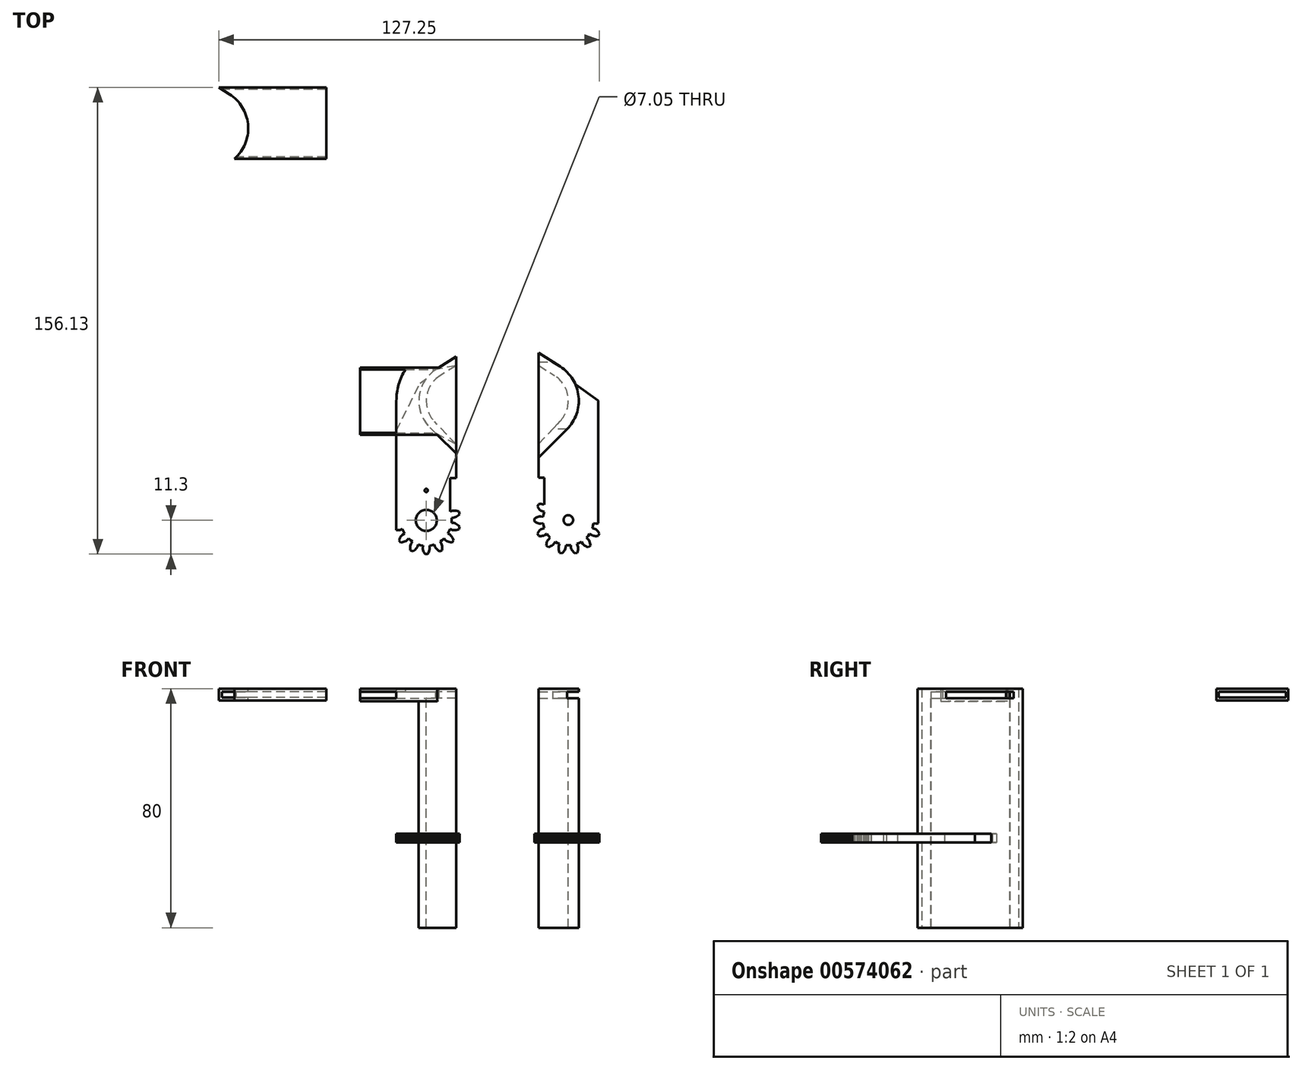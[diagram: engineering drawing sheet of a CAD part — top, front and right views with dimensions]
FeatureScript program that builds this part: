
annotation { "Feature Type Name" : "Feature", "Feature Type Description" : "" }
export const myFeature = defineFeature(function(context is Context, id is Id, definition is map)
    precondition{}
    {
        {
            var Q0;
            Q0=qCreatedBy(makeId("Top.planeOp"),FACE);
            var sketch = newSketch(context, id + "F0", { "sketchPlane" : qUnion([Q0])});
            skLineSegment(sketch, "E0", {"start": v(-11.89, -38.22) * mm, "end": v(-11.08, -38.37) * mm});
            skLineSegment(sketch, "E1", {"start": v(-11.08, -38.37) * mm, "end": v(-11.18, -39.18) * mm});
            skLineSegment(sketch, "E2", {"start": v(-11.18, -39.18) * mm, "end": v(-11.15, -39.59) * mm});
            skLineSegment(sketch, "E3", {"start": v(-11.15, -39.59) * mm, "end": v(-11.05, -40) * mm});
            skLineSegment(sketch, "E4", {"start": v(-11.05, -40) * mm, "end": v(-10.9, -40.42) * mm});
            skLineSegment(sketch, "E5", {"start": v(-10.9, -40.42) * mm, "end": v(-10.7, -40.84) * mm});
            skLineSegment(sketch, "E6", {"start": v(-10.7, -40.84) * mm, "end": v(-10.46, -41.25) * mm});
            skLineSegment(sketch, "E7", {"start": v(-10.46, -41.25) * mm, "end": v(-9.54, -41.25) * mm});
            skLineSegment(sketch, "E8", {"start": v(-9.54, -41.25) * mm, "end": v(-9.3, -40.84) * mm});
            skLineSegment(sketch, "E9", {"start": v(-9.3, -40.84) * mm, "end": v(-9.1, -40.42) * mm});
            skLineSegment(sketch, "E10", {"start": v(-9.1, -40.42) * mm, "end": v(-8.95, -40) * mm});
            skLineSegment(sketch, "E11", {"start": v(-8.95, -40) * mm, "end": v(-8.85, -39.59) * mm});
            skLineSegment(sketch, "E12", {"start": v(-8.85, -39.59) * mm, "end": v(-8.82, -39.18) * mm});
            skLineSegment(sketch, "E13", {"start": v(-8.82, -39.18) * mm, "end": v(-8.92, -38.37) * mm});
            skLineSegment(sketch, "E14", {"start": v(-8.92, -38.37) * mm, "end": v(-8.11, -38.22) * mm});
            skLineSegment(sketch, "E15", {"start": v(-8.11, -38.22) * mm, "end": v(-8.11, -38.22) * mm});
            skLineSegment(sketch, "E16", {"start": v(-8.11, -38.22) * mm, "end": v(-7.32, -38) * mm});
            skLineSegment(sketch, "E17", {"start": v(-7.32, -38) * mm, "end": v(-7.06, -38.78) * mm});
            skLineSegment(sketch, "E18", {"start": v(-7.06, -38.78) * mm, "end": v(-6.86, -39.13) * mm});
            skLineSegment(sketch, "E19", {"start": v(-6.86, -39.13) * mm, "end": v(-6.58, -39.46) * mm});
            skLineSegment(sketch, "E20", {"start": v(-6.58, -39.46) * mm, "end": v(-6.26, -39.77) * mm});
            skLineSegment(sketch, "E21", {"start": v(-6.26, -39.77) * mm, "end": v(-5.9, -40.06) * mm});
            skLineSegment(sketch, "E22", {"start": v(-5.9, -40.06) * mm, "end": v(-5.5, -40.33) * mm});
            skLineSegment(sketch, "E23", {"start": v(-5.5, -40.33) * mm, "end": v(-4.68, -39.94) * mm});
            skLineSegment(sketch, "E24", {"start": v(-4.68, -39.94) * mm, "end": v(-4.65, -39.46) * mm});
            skLineSegment(sketch, "E25", {"start": v(-4.65, -39.46) * mm, "end": v(-4.65, -39) * mm});
            skLineSegment(sketch, "E26", {"start": v(-4.7, -38.55) * mm, "end": v(-4.78, -38.13) * mm});
            skLineSegment(sketch, "E27", {"start": v(-4.78, -38.13) * mm, "end": v(-4.93, -37.75) * mm});
            skLineSegment(sketch, "E28", {"start": v(-4.93, -37.75) * mm, "end": v(-5.38, -37.07) * mm});
            skLineSegment(sketch, "E29", {"start": v(-4.09, -36.04) * mm, "end": v(-3.52, -36.62) * mm});
            skLineSegment(sketch, "E30", {"start": v(-3.18, -36.86) * mm, "end": v(-2.8, -37.04) * mm});
            skLineSegment(sketch, "E31", {"start": v(-2.37, -37.18) * mm, "end": v(-1.92, -37.28) * mm});
            skLineSegment(sketch, "E32", {"start": v(-1.05, -36.2) * mm, "end": v(-1.25, -35.78) * mm});
            skLineSegment(sketch, "E33", {"start": v(-1.25, -35.78) * mm, "end": v(-1.49, -35.4) * mm});
            skLineSegment(sketch, "E34", {"start": v(-2.05, -34.78) * mm, "end": v(-2.75, -34.36) * mm});
            skLineSegment(sketch, "E35", {"start": v(-2.03, -32.87) * mm, "end": v(-1.27, -33.15) * mm});
            skLineSegment(sketch, "E36", {"start": v(-20, -33.15) * mm, "end": v(-19.57, -33.2) * mm});
            skLineSegment(sketch, "E37", {"start": v(-19.57, -33.2) * mm, "end": v(-19.14, -33.22) * mm});
            skLineSegment(sketch, "E38", {"start": v(-19.14, -33.22) * mm, "end": v(-18.73, -33.15) * mm});
            skLineSegment(sketch, "E39", {"start": v(-18.73, -33.15) * mm, "end": v(-17.97, -32.87) * mm});
            skLineSegment(sketch, "E40", {"start": v(-17.97, -32.87) * mm, "end": v(-17.64, -33.63) * mm});
            skLineSegment(sketch, "E41", {"start": v(-17.64, -33.63) * mm, "end": v(-17.65, -33.63) * mm});
            skLineSegment(sketch, "E42", {"start": v(-17.65, -33.63) * mm, "end": v(-17.25, -34.36) * mm});
            skLineSegment(sketch, "E43", {"start": v(-17.25, -34.36) * mm, "end": v(-17.95, -34.78) * mm});
            skLineSegment(sketch, "E44", {"start": v(-17.95, -34.78) * mm, "end": v(-18.25, -35.06) * mm});
            skLineSegment(sketch, "E45", {"start": v(-18.25, -35.06) * mm, "end": v(-18.51, -35.4) * mm});
            skLineSegment(sketch, "E46", {"start": v(-18.51, -35.4) * mm, "end": v(-18.75, -35.78) * mm});
            skLineSegment(sketch, "E47", {"start": v(-18.75, -35.78) * mm, "end": v(-18.95, -36.2) * mm});
            skLineSegment(sketch, "E48", {"start": v(-18.95, -36.2) * mm, "end": v(-19.12, -36.64) * mm});
            skLineSegment(sketch, "E49", {"start": v(-19.12, -36.64) * mm, "end": v(-18.55, -37.36) * mm});
            skLineSegment(sketch, "E50", {"start": v(-18.55, -37.36) * mm, "end": v(-18.08, -37.28) * mm});
            skLineSegment(sketch, "E51", {"start": v(-18.08, -37.28) * mm, "end": v(-17.63, -37.18) * mm});
            skLineSegment(sketch, "E52", {"start": v(-17.63, -37.18) * mm, "end": v(-17.2, -37.04) * mm});
            skLineSegment(sketch, "E53", {"start": v(-17.2, -37.04) * mm, "end": v(-16.82, -36.86) * mm});
            skLineSegment(sketch, "E54", {"start": v(-16.82, -36.86) * mm, "end": v(-16.48, -36.62) * mm});
            skLineSegment(sketch, "E55", {"start": v(-16.48, -36.62) * mm, "end": v(-15.91, -36.04) * mm});
            skLineSegment(sketch, "E56", {"start": v(-15.91, -36.04) * mm, "end": v(-15.3, -36.58) * mm});
            skLineSegment(sketch, "E57", {"start": v(-15.3, -36.58) * mm, "end": v(-15.3, -36.58) * mm});
            skLineSegment(sketch, "E58", {"start": v(-15.3, -36.58) * mm, "end": v(-14.62, -37.07) * mm});
            skLineSegment(sketch, "E59", {"start": v(-14.62, -37.07) * mm, "end": v(-15.07, -37.75) * mm});
            skLineSegment(sketch, "E60", {"start": v(-15.07, -37.75) * mm, "end": v(-15.22, -38.13) * mm});
            skLineSegment(sketch, "E61", {"start": v(-15.22, -38.13) * mm, "end": v(-15.3, -38.55) * mm});
            skLineSegment(sketch, "E62", {"start": v(-15.3, -38.55) * mm, "end": v(-15.35, -39) * mm});
            skLineSegment(sketch, "E63", {"start": v(-15.35, -39) * mm, "end": v(-15.35, -39.46) * mm});
            skLineSegment(sketch, "E64", {"start": v(-15.35, -39.46) * mm, "end": v(-15.32, -39.94) * mm});
            skLineSegment(sketch, "E65", {"start": v(-15.32, -39.94) * mm, "end": v(-14.5, -40.33) * mm});
            skLineSegment(sketch, "E66", {"start": v(-14.5, -40.33) * mm, "end": v(-14.1, -40.06) * mm});
            skLineSegment(sketch, "E67", {"start": v(-14.1, -40.06) * mm, "end": v(-13.74, -39.77) * mm});
            skLineSegment(sketch, "E68", {"start": v(-13.74, -39.77) * mm, "end": v(-13.42, -39.46) * mm});
            skLineSegment(sketch, "E69", {"start": v(-13.42, -39.46) * mm, "end": v(-13.14, -39.13) * mm});
            skLineSegment(sketch, "E70", {"start": v(-13.14, -39.13) * mm, "end": v(-12.94, -38.78) * mm});
            skLineSegment(sketch, "E71", {"start": v(-12.94, -38.78) * mm, "end": v(-12.68, -38) * mm});
            skLineSegment(sketch, "E72", {"start": v(-12.68, -38) * mm, "end": v(-11.89, -38.22) * mm});
            skLineSegment(sketch, "E73", {"start": v(-11.89, -38.22) * mm, "end": v(-11.89, -38.22) * mm});
            skLineSegment(sketch, "E74", {"start": v(-2, -27.02) * mm, "end": v(-2, -15.8) * mm});
            skLineSegment(sketch, "E75", {"start": v(-4.65, -39) * mm, "end": v(-4.7, -38.55) * mm});
            skLineSegment(sketch, "E76", {"start": v(-5.38, -37.07) * mm, "end": v(-4.7, -36.58) * mm});
            skLineSegment(sketch, "E77", {"start": v(-4.7, -36.58) * mm, "end": v(-4.7, -36.58) * mm});
            skLineSegment(sketch, "E78", {"start": v(-4.7, -36.58) * mm, "end": v(-4.09, -36.04) * mm});
            skLineSegment(sketch, "E79", {"start": v(-3.52, -36.62) * mm, "end": v(-3.18, -36.86) * mm});
            skLineSegment(sketch, "E80", {"start": v(-2.8, -37.04) * mm, "end": v(-2.37, -37.18) * mm});
            skLineSegment(sketch, "E81", {"start": v(-1.92, -37.28) * mm, "end": v(-1.45, -37.36) * mm});
            skLineSegment(sketch, "E82", {"start": v(-1.45, -37.36) * mm, "end": v(-0.88, -36.64) * mm});
            skLineSegment(sketch, "E83", {"start": v(-0.88, -36.64) * mm, "end": v(-1.05, -36.2) * mm});
            skLineSegment(sketch, "E84", {"start": v(-1.49, -35.4) * mm, "end": v(-1.75, -35.06) * mm});
            skLineSegment(sketch, "E85", {"start": v(-1.75, -35.06) * mm, "end": v(-2.05, -34.78) * mm});
            skLineSegment(sketch, "E86", {"start": v(-2.75, -34.36) * mm, "end": v(-2.35, -33.63) * mm});
            skLineSegment(sketch, "E87", {"start": v(-2.35, -33.63) * mm, "end": v(-2.36, -33.63) * mm});
            skLineSegment(sketch, "E88", {"start": v(-2.36, -33.63) * mm, "end": v(-2.03, -32.87) * mm});
            skLineSegment(sketch, "E89", {"start": v(-1.27, -33.15) * mm, "end": v(-0.86, -33.22) * mm});
            skLineSegment(sketch, "E90", {"start": v(-0.86, -33.22) * mm, "end": v(-0.43, -33.2) * mm});
            skLineSegment(sketch, "E91", {"start": v(-0.43, -33.2) * mm, "end": v(0, -33.15) * mm});
            skLineSegment(sketch, "E92", {"start": v(0, -33.15) * mm, "end": v(0.46, -33.05) * mm});
            skLineSegment(sketch, "E93", {"start": v(0.46, -33.05) * mm, "end": v(0.92, -32.91) * mm});
            skLineSegment(sketch, "E94", {"start": v(0.92, -32.91) * mm, "end": v(1.12, -32.02) * mm});
            skLineSegment(sketch, "E95", {"start": v(1.12, -32.02) * mm, "end": v(0.77, -31.7) * mm});
            skLineSegment(sketch, "E96", {"start": v(0.77, -31.7) * mm, "end": v(0.4, -31.4) * mm});
            skLineSegment(sketch, "E97", {"start": v(0.4, -31.4) * mm, "end": v(0.03, -31.16) * mm});
            skLineSegment(sketch, "E98", {"start": v(0.03, -31.16) * mm, "end": v(-0.35, -30.97) * mm});
            skLineSegment(sketch, "E99", {"start": v(-0.35, -30.97) * mm, "end": v(-0.74, -30.85) * mm});
            skLineSegment(sketch, "E100", {"start": v(-0.74, -30.85) * mm, "end": v(-1.55, -30.77) * mm});
            skLineSegment(sketch, "E101", {"start": v(-1.55, -30.77) * mm, "end": v(-1.51, -29.95) * mm});
            skLineSegment(sketch, "E102", {"start": v(-1.51, -29.95) * mm, "end": v(-1.51, -29.95) * mm});
            skLineSegment(sketch, "E103", {"start": v(-1.51, -29.95) * mm, "end": v(-1.55, -29.13) * mm});
            skLineSegment(sketch, "E104", {"start": v(-1.55, -29.13) * mm, "end": v(-0.74, -29.05) * mm});
            skLineSegment(sketch, "E105", {"start": v(-0.74, -29.05) * mm, "end": v(-0.35, -28.93) * mm});
            skLineSegment(sketch, "E106", {"start": v(-0.35, -28.93) * mm, "end": v(0.03, -28.74) * mm});
            skLineSegment(sketch, "E107", {"start": v(0.03, -28.74) * mm, "end": v(0.4, -28.5) * mm});
            skLineSegment(sketch, "E108", {"start": v(0.4, -28.5) * mm, "end": v(0.77, -28.2) * mm});
            skLineSegment(sketch, "E109", {"start": v(0.77, -28.2) * mm, "end": v(1.12, -27.88) * mm});
            skLineSegment(sketch, "E110", {"start": v(1.12, -27.88) * mm, "end": v(0.92, -26.99) * mm});
            skLineSegment(sketch, "E111", {"start": v(0.92, -26.99) * mm, "end": v(0.46, -26.85) * mm});
            skLineSegment(sketch, "E112", {"start": v(0.46, -26.85) * mm, "end": v(0, -26.75) * mm});
            skLineSegment(sketch, "E113", {"start": v(0, -26.75) * mm, "end": v(-0.43, -26.69) * mm});
            skLineSegment(sketch, "E114", {"start": v(-0.43, -26.69) * mm, "end": v(-0.86, -26.68) * mm});
            skLineSegment(sketch, "E115", {"start": v(-0.86, -26.68) * mm, "end": v(-1.27, -26.75) * mm});
            skLineSegment(sketch, "E116", {"start": v(-1.27, -26.75) * mm, "end": v(-2, -27.02) * mm});
            skLineSegment(sketch, "E117", {"start": v(45.78, -31.73) * mm, "end": v(45.92, -30.92) * mm});
            skLineSegment(sketch, "E118", {"start": v(45.92, -30.92) * mm, "end": v(46.73, -31.02) * mm});
            skLineSegment(sketch, "E119", {"start": v(46.73, -31.02) * mm, "end": v(47.14, -31) * mm});
            skLineSegment(sketch, "E120", {"start": v(47.14, -31) * mm, "end": v(47.5, -30.9) * mm});
            skLineSegment(sketch, "E121", {"start": v(27.87, -31) * mm, "end": v(28.28, -31.02) * mm});
            skLineSegment(sketch, "E122", {"start": v(29.1, -30.92) * mm, "end": v(29.23, -31.73) * mm});
            skLineSegment(sketch, "E123", {"start": v(28.68, -32.78) * mm, "end": v(28.33, -32.99) * mm});
            skLineSegment(sketch, "E124", {"start": v(27.68, -33.58) * mm, "end": v(27.4, -33.94) * mm});
            skLineSegment(sketch, "E125", {"start": v(28.46, -35.2) * mm, "end": v(28.9, -35.15) * mm});
            skLineSegment(sketch, "E126", {"start": v(28.9, -35.15) * mm, "end": v(29.32, -35.06) * mm});
            skLineSegment(sketch, "E127", {"start": v(29.32, -35.06) * mm, "end": v(29.7, -34.9) * mm});
            skLineSegment(sketch, "E128", {"start": v(29.7, -34.9) * mm, "end": v(30.4, -34.46) * mm});
            skLineSegment(sketch, "E129", {"start": v(30.4, -34.46) * mm, "end": v(30.87, -35.13) * mm});
            skLineSegment(sketch, "E130", {"start": v(30.87, -35.13) * mm, "end": v(30.87, -35.13) * mm});
            skLineSegment(sketch, "E131", {"start": v(31.42, -35.75) * mm, "end": v(30.83, -36.32) * mm});
            skLineSegment(sketch, "E132", {"start": v(30.17, -37.92) * mm, "end": v(30.1, -38.4) * mm});
            skLineSegment(sketch, "E133", {"start": v(30.1, -38.4) * mm, "end": v(30.82, -38.96) * mm});
            skLineSegment(sketch, "E134", {"start": v(30.82, -38.96) * mm, "end": v(31.26, -38.8) * mm});
            skLineSegment(sketch, "E135", {"start": v(31.68, -38.59) * mm, "end": v(32.06, -38.35) * mm});
            skLineSegment(sketch, "E136", {"start": v(32.06, -38.35) * mm, "end": v(32.4, -38.1) * mm});
            skLineSegment(sketch, "E137", {"start": v(32.68, -37.8) * mm, "end": v(33.1, -37.1) * mm});
            skLineSegment(sketch, "E138", {"start": v(33.1, -37.1) * mm, "end": v(33.83, -37.49) * mm});
            skLineSegment(sketch, "E139", {"start": v(33.83, -37.49) * mm, "end": v(33.83, -37.49) * mm});
            skLineSegment(sketch, "E140", {"start": v(34.59, -37.8) * mm, "end": v(34.3, -38.58) * mm});
            skLineSegment(sketch, "E141", {"start": v(34.4, -40.3) * mm, "end": v(34.55, -40.76) * mm});
            skLineSegment(sketch, "E142", {"start": v(35.44, -40.96) * mm, "end": v(35.76, -40.61) * mm});
            skLineSegment(sketch, "E143", {"start": v(36.05, -40.25) * mm, "end": v(36.3, -39.88) * mm});
            skLineSegment(sketch, "E144", {"start": v(36.68, -38.29) * mm, "end": v(37.5, -38.33) * mm});
            skLineSegment(sketch, "E145", {"start": v(37.5, -38.33) * mm, "end": v(37.5, -38.33) * mm});
            skLineSegment(sketch, "E146", {"start": v(37.5, -38.33) * mm, "end": v(38.33, -38.29) * mm});
            skLineSegment(sketch, "E147", {"start": v(38.33, -38.29) * mm, "end": v(38.41, -39.1) * mm});
            skLineSegment(sketch, "E148", {"start": v(38.41, -39.1) * mm, "end": v(38.53, -39.5) * mm});
            skLineSegment(sketch, "E149", {"start": v(38.53, -39.5) * mm, "end": v(38.72, -39.88) * mm});
            skLineSegment(sketch, "E150", {"start": v(38.72, -39.88) * mm, "end": v(38.96, -40.25) * mm});
            skLineSegment(sketch, "E151", {"start": v(38.96, -40.25) * mm, "end": v(39.25, -40.61) * mm});
            skLineSegment(sketch, "E152", {"start": v(39.25, -40.61) * mm, "end": v(39.58, -40.96) * mm});
            skLineSegment(sketch, "E153", {"start": v(39.58, -40.96) * mm, "end": v(40.47, -40.76) * mm});
            skLineSegment(sketch, "E154", {"start": v(40.47, -40.76) * mm, "end": v(40.61, -40.3) * mm});
            skLineSegment(sketch, "E155", {"start": v(40.61, -40.3) * mm, "end": v(40.71, -39.85) * mm});
            skLineSegment(sketch, "E156", {"start": v(40.71, -39.85) * mm, "end": v(40.77, -39.4) * mm});
            skLineSegment(sketch, "E157", {"start": v(40.77, -39.4) * mm, "end": v(40.77, -38.98) * mm});
            skLineSegment(sketch, "E158", {"start": v(40.77, -38.98) * mm, "end": v(40.7, -38.58) * mm});
            skLineSegment(sketch, "E159", {"start": v(40.7, -38.58) * mm, "end": v(40.43, -37.8) * mm});
            skLineSegment(sketch, "E160", {"start": v(40.43, -37.8) * mm, "end": v(41.19, -37.49) * mm});
            skLineSegment(sketch, "E161", {"start": v(41.19, -37.49) * mm, "end": v(41.19, -37.49) * mm});
            skLineSegment(sketch, "E162", {"start": v(41.19, -37.49) * mm, "end": v(41.91, -37.1) * mm});
            skLineSegment(sketch, "E163", {"start": v(41.91, -37.1) * mm, "end": v(42.34, -37.8) * mm});
            skLineSegment(sketch, "E164", {"start": v(42.34, -37.8) * mm, "end": v(42.62, -38.1) * mm});
            skLineSegment(sketch, "E165", {"start": v(42.62, -38.1) * mm, "end": v(42.95, -38.35) * mm});
            skLineSegment(sketch, "E166", {"start": v(42.95, -38.35) * mm, "end": v(43.33, -38.59) * mm});
            skLineSegment(sketch, "E167", {"start": v(43.33, -38.59) * mm, "end": v(43.75, -38.8) * mm});
            skLineSegment(sketch, "E168", {"start": v(43.75, -38.8) * mm, "end": v(44.2, -38.96) * mm});
            skLineSegment(sketch, "E169", {"start": v(44.2, -38.96) * mm, "end": v(44.91, -38.4) * mm});
            skLineSegment(sketch, "E170", {"start": v(44.91, -38.4) * mm, "end": v(44.84, -37.92) * mm});
            skLineSegment(sketch, "E171", {"start": v(44.84, -37.92) * mm, "end": v(44.74, -37.47) * mm});
            skLineSegment(sketch, "E172", {"start": v(44.74, -37.47) * mm, "end": v(44.6, -37.05) * mm});
            skLineSegment(sketch, "E173", {"start": v(44.6, -37.05) * mm, "end": v(44.41, -36.66) * mm});
            skLineSegment(sketch, "E174", {"start": v(44.41, -36.66) * mm, "end": v(44.18, -36.32) * mm});
            skLineSegment(sketch, "E175", {"start": v(44.18, -36.32) * mm, "end": v(43.6, -35.75) * mm});
            skLineSegment(sketch, "E176", {"start": v(43.6, -35.75) * mm, "end": v(44.14, -35.13) * mm});
            skLineSegment(sketch, "E177", {"start": v(44.14, -35.13) * mm, "end": v(44.14, -35.13) * mm});
            skLineSegment(sketch, "E178", {"start": v(44.14, -35.13) * mm, "end": v(44.62, -34.46) * mm});
            skLineSegment(sketch, "E179", {"start": v(44.62, -34.46) * mm, "end": v(45.3, -34.9) * mm});
            skLineSegment(sketch, "E180", {"start": v(45.3, -34.9) * mm, "end": v(45.69, -35.06) * mm});
            skLineSegment(sketch, "E181", {"start": v(45.69, -35.06) * mm, "end": v(46.1, -35.15) * mm});
            skLineSegment(sketch, "E182", {"start": v(46.1, -35.15) * mm, "end": v(46.55, -35.2) * mm});
            skLineSegment(sketch, "E183", {"start": v(46.55, -35.2) * mm, "end": v(47.01, -35.2) * mm});
            skLineSegment(sketch, "E184", {"start": v(47.01, -35.2) * mm, "end": v(47.5, -35.16) * mm});
            skLineSegment(sketch, "E185", {"start": v(47.5, -35.16) * mm, "end": v(47.9, -34.33) * mm});
            skLineSegment(sketch, "E186", {"start": v(47.9, -34.33) * mm, "end": v(47.62, -33.94) * mm});
            skLineSegment(sketch, "E187", {"start": v(47.62, -33.94) * mm, "end": v(47.33, -33.58) * mm});
            skLineSegment(sketch, "E188", {"start": v(47.33, -33.58) * mm, "end": v(47.02, -33.26) * mm});
            skLineSegment(sketch, "E189", {"start": v(47.02, -33.26) * mm, "end": v(46.69, -32.99) * mm});
            skLineSegment(sketch, "E190", {"start": v(46.69, -32.99) * mm, "end": v(46.33, -32.78) * mm});
            skLineSegment(sketch, "E191", {"start": v(46.33, -32.78) * mm, "end": v(45.56, -32.52) * mm});
            skLineSegment(sketch, "E192", {"start": v(45.56, -32.52) * mm, "end": v(45.78, -31.73) * mm});
            skLineSegment(sketch, "E193", {"start": v(45.78, -31.73) * mm, "end": v(45.78, -31.73) * mm});
            skLineSegment(sketch, "E194", {"start": v(29.5, -24.7) * mm, "end": v(29.5, -15.7) * mm});
            skLineSegment(sketch, "E195", {"start": v(47.5, -30.9) * mm, "end": v(47.5, 10.1) * mm});
            skLineSegment(sketch, "E196", {"start": v(29.5, -24.7) * mm, "end": v(29.32, -24.62) * mm});
            skLineSegment(sketch, "E197", {"start": v(29.32, -24.62) * mm, "end": v(28.9, -24.53) * mm});
            skLineSegment(sketch, "E198", {"start": v(28.9, -24.53) * mm, "end": v(28.46, -24.5) * mm});
            skLineSegment(sketch, "E199", {"start": v(28.46, -24.5) * mm, "end": v(28, -24.49) * mm});
            skLineSegment(sketch, "E200", {"start": v(28, -24.49) * mm, "end": v(27.52, -24.53) * mm});
            skLineSegment(sketch, "E201", {"start": v(27.52, -24.53) * mm, "end": v(27.12, -25.35) * mm});
            skLineSegment(sketch, "E202", {"start": v(27.12, -25.35) * mm, "end": v(27.4, -25.75) * mm});
            skLineSegment(sketch, "E203", {"start": v(27.4, -25.75) * mm, "end": v(27.68, -26.1) * mm});
            skLineSegment(sketch, "E204", {"start": v(27.68, -26.1) * mm, "end": v(28, -26.43) * mm});
            skLineSegment(sketch, "E205", {"start": v(28, -26.43) * mm, "end": v(28.33, -26.7) * mm});
            skLineSegment(sketch, "E206", {"start": v(28.33, -26.7) * mm, "end": v(28.68, -26.9) * mm});
            skLineSegment(sketch, "E207", {"start": v(28.68, -26.9) * mm, "end": v(29.46, -27.16) * mm});
            skLineSegment(sketch, "E208", {"start": v(29.46, -27.16) * mm, "end": v(29.23, -27.95) * mm});
            skLineSegment(sketch, "E209", {"start": v(29.23, -27.95) * mm, "end": v(29.23, -27.95) * mm});
            skLineSegment(sketch, "E210", {"start": v(29.23, -27.95) * mm, "end": v(29.1, -28.77) * mm});
            skLineSegment(sketch, "E211", {"start": v(29.1, -28.77) * mm, "end": v(28.28, -28.66) * mm});
            skLineSegment(sketch, "E212", {"start": v(28.28, -28.66) * mm, "end": v(27.87, -28.7) * mm});
            skLineSegment(sketch, "E213", {"start": v(27.87, -28.7) * mm, "end": v(27.45, -28.8) * mm});
            skLineSegment(sketch, "E214", {"start": v(27.45, -28.8) * mm, "end": v(27.04, -28.94) * mm});
            skLineSegment(sketch, "E215", {"start": v(27.04, -28.94) * mm, "end": v(26.62, -29.14) * mm});
            skLineSegment(sketch, "E216", {"start": v(26.62, -29.14) * mm, "end": v(26.2, -29.38) * mm});
            skLineSegment(sketch, "E217", {"start": v(26.2, -30.3) * mm, "end": v(26.62, -30.54) * mm});
            skLineSegment(sketch, "E218", {"start": v(26.62, -30.54) * mm, "end": v(27.04, -30.74) * mm});
            skLineSegment(sketch, "E219", {"start": v(27.04, -30.74) * mm, "end": v(27.45, -30.9) * mm});
            skLineSegment(sketch, "E220", {"start": v(27.45, -30.9) * mm, "end": v(27.87, -31) * mm});
            skLineSegment(sketch, "E221", {"start": v(28.28, -31.02) * mm, "end": v(29.1, -30.92) * mm});
            skLineSegment(sketch, "E222", {"start": v(29.23, -31.73) * mm, "end": v(29.23, -31.73) * mm});
            skLineSegment(sketch, "E223", {"start": v(29.23, -31.73) * mm, "end": v(29.46, -32.52) * mm});
            skLineSegment(sketch, "E224", {"start": v(29.46, -32.52) * mm, "end": v(28.68, -32.78) * mm});
            skLineSegment(sketch, "E225", {"start": v(28.33, -32.99) * mm, "end": v(28, -33.26) * mm});
            skLineSegment(sketch, "E226", {"start": v(28, -33.26) * mm, "end": v(27.68, -33.58) * mm});
            skLineSegment(sketch, "E227", {"start": v(27.4, -33.94) * mm, "end": v(27.12, -34.33) * mm});
            skLineSegment(sketch, "E228", {"start": v(27.12, -34.33) * mm, "end": v(27.52, -35.16) * mm});
            skLineSegment(sketch, "E229", {"start": v(27.52, -35.16) * mm, "end": v(28, -35.2) * mm});
            skLineSegment(sketch, "E230", {"start": v(28, -35.2) * mm, "end": v(28.46, -35.2) * mm});
            skLineSegment(sketch, "E231", {"start": v(30.87, -35.13) * mm, "end": v(31.42, -35.75) * mm});
            skLineSegment(sketch, "E232", {"start": v(30.83, -36.32) * mm, "end": v(30.6, -36.66) * mm});
            skLineSegment(sketch, "E233", {"start": v(30.6, -36.66) * mm, "end": v(30.42, -37.05) * mm});
            skLineSegment(sketch, "E234", {"start": v(30.42, -37.05) * mm, "end": v(30.28, -37.47) * mm});
            skLineSegment(sketch, "E235", {"start": v(30.28, -37.47) * mm, "end": v(30.17, -37.92) * mm});
            skLineSegment(sketch, "E236", {"start": v(31.26, -38.8) * mm, "end": v(31.68, -38.59) * mm});
            skLineSegment(sketch, "E237", {"start": v(32.4, -38.1) * mm, "end": v(32.68, -37.8) * mm});
            skLineSegment(sketch, "E238", {"start": v(33.83, -37.49) * mm, "end": v(34.59, -37.8) * mm});
            skLineSegment(sketch, "E239", {"start": v(34.3, -38.58) * mm, "end": v(34.24, -38.98) * mm});
            skLineSegment(sketch, "E240", {"start": v(34.24, -38.98) * mm, "end": v(34.25, -39.4) * mm});
            skLineSegment(sketch, "E241", {"start": v(34.25, -39.4) * mm, "end": v(34.3, -39.85) * mm});
            skLineSegment(sketch, "E242", {"start": v(34.3, -39.85) * mm, "end": v(34.4, -40.3) * mm});
            skLineSegment(sketch, "E243", {"start": v(34.55, -40.76) * mm, "end": v(35.44, -40.96) * mm});
            skLineSegment(sketch, "E244", {"start": v(35.76, -40.61) * mm, "end": v(36.05, -40.25) * mm});
            skLineSegment(sketch, "E245", {"start": v(36.3, -39.88) * mm, "end": v(36.48, -39.5) * mm});
            skLineSegment(sketch, "E246", {"start": v(36.48, -39.5) * mm, "end": v(36.6, -39.1) * mm});
            skLineSegment(sketch, "E247", {"start": v(36.6, -39.1) * mm, "end": v(36.68, -38.29) * mm});
            skLineSegment(sketch, "E248", {"start": v(26.2, -29.38) * mm, "end": v(26.2, -30.3) * mm});
            skCircle(sketch, "E249", {"center": v(37.5, -29.84) * mm, "radius": 1.6 * mm});
            skCircle(sketch, "E250", {"center": v(-10, -29.95) * mm, "radius": 3.52 * mm});
            skCircle(sketch, "E251", {"center": v(-10, -19.95) * mm, "radius": 0.55 * mm});
            skLineSegment(sketch, "E252", {"start": v(97.08, -42.45) * mm, "end": v(97.9, -42.59) * mm});
            skLineSegment(sketch, "E253", {"start": v(97.9, -42.59) * mm, "end": v(97.8, -43.4) * mm});
            skLineSegment(sketch, "E254", {"start": v(97.8, -43.4) * mm, "end": v(97.82, -43.8) * mm});
            skLineSegment(sketch, "E255", {"start": v(97.82, -43.8) * mm, "end": v(97.92, -44.23) * mm});
            skLineSegment(sketch, "E256", {"start": v(97.92, -44.23) * mm, "end": v(98.07, -44.64) * mm});
            skLineSegment(sketch, "E257", {"start": v(98.07, -44.64) * mm, "end": v(98.27, -45.06) * mm});
            skLineSegment(sketch, "E258", {"start": v(98.27, -45.06) * mm, "end": v(98.51, -45.48) * mm});
            skLineSegment(sketch, "E259", {"start": v(98.51, -45.48) * mm, "end": v(99.43, -45.48) * mm});
            skLineSegment(sketch, "E260", {"start": v(99.43, -45.48) * mm, "end": v(99.67, -45.06) * mm});
            skLineSegment(sketch, "E261", {"start": v(99.67, -45.06) * mm, "end": v(99.87, -44.64) * mm});
            skLineSegment(sketch, "E262", {"start": v(99.87, -44.64) * mm, "end": v(100.02, -44.23) * mm});
            skLineSegment(sketch, "E263", {"start": v(100.02, -44.23) * mm, "end": v(100.12, -43.8) * mm});
            skLineSegment(sketch, "E264", {"start": v(100.12, -43.8) * mm, "end": v(100.15, -43.4) * mm});
            skLineSegment(sketch, "E265", {"start": v(100.15, -43.4) * mm, "end": v(100.05, -42.59) * mm});
            skLineSegment(sketch, "E266", {"start": v(100.05, -42.59) * mm, "end": v(100.86, -42.45) * mm});
            skLineSegment(sketch, "E267", {"start": v(100.86, -42.45) * mm, "end": v(100.86, -42.45) * mm});
            skLineSegment(sketch, "E268", {"start": v(100.86, -42.45) * mm, "end": v(101.65, -42.22) * mm});
            skLineSegment(sketch, "E269", {"start": v(101.65, -42.22) * mm, "end": v(101.91, -43) * mm});
            skLineSegment(sketch, "E270", {"start": v(101.91, -43) * mm, "end": v(102.12, -43.35) * mm});
            skLineSegment(sketch, "E271", {"start": v(102.12, -43.35) * mm, "end": v(102.39, -43.68) * mm});
            skLineSegment(sketch, "E272", {"start": v(102.39, -43.68) * mm, "end": v(102.7, -44) * mm});
            skLineSegment(sketch, "E273", {"start": v(102.7, -44) * mm, "end": v(103.07, -44.29) * mm});
            skLineSegment(sketch, "E274", {"start": v(103.07, -44.29) * mm, "end": v(103.46, -44.56) * mm});
            skLineSegment(sketch, "E275", {"start": v(103.46, -44.56) * mm, "end": v(104.29, -44.16) * mm});
            skLineSegment(sketch, "E276", {"start": v(104.29, -44.16) * mm, "end": v(104.32, -43.68) * mm});
            skLineSegment(sketch, "E277", {"start": v(104.32, -43.68) * mm, "end": v(104.32, -43.22) * mm});
            skLineSegment(sketch, "E278", {"start": v(104.28, -42.77) * mm, "end": v(104.19, -42.36) * mm});
            skLineSegment(sketch, "E279", {"start": v(104.19, -42.36) * mm, "end": v(104.04, -41.97) * mm});
            skLineSegment(sketch, "E280", {"start": v(104.04, -41.97) * mm, "end": v(103.6, -41.29) * mm});
            skLineSegment(sketch, "E281", {"start": v(104.88, -40.26) * mm, "end": v(105.45, -40.85) * mm});
            skLineSegment(sketch, "E282", {"start": v(105.79, -41.08) * mm, "end": v(106.18, -41.26) * mm});
            skLineSegment(sketch, "E283", {"start": v(106.6, -41.4) * mm, "end": v(107.05, -41.5) * mm});
            skLineSegment(sketch, "E284", {"start": v(107.92, -40.42) * mm, "end": v(107.72, -40) * mm});
            skLineSegment(sketch, "E285", {"start": v(107.72, -40) * mm, "end": v(107.48, -39.62) * mm});
            skLineSegment(sketch, "E286", {"start": v(106.92, -39) * mm, "end": v(106.22, -38.58) * mm});
            skLineSegment(sketch, "E287", {"start": v(106.94, -37.1) * mm, "end": v(107.7, -37.38) * mm});
            skLineSegment(sketch, "E288", {"start": v(88.96, -37.38) * mm, "end": v(89.4, -37.43) * mm});
            skLineSegment(sketch, "E289", {"start": v(89.4, -37.43) * mm, "end": v(89.83, -37.44) * mm});
            skLineSegment(sketch, "E290", {"start": v(89.83, -37.44) * mm, "end": v(90.24, -37.38) * mm});
            skLineSegment(sketch, "E291", {"start": v(90.24, -37.38) * mm, "end": v(91, -37.1) * mm});
            skLineSegment(sketch, "E292", {"start": v(91, -37.1) * mm, "end": v(91.33, -37.85) * mm});
            skLineSegment(sketch, "E293", {"start": v(91.33, -37.85) * mm, "end": v(91.33, -37.85) * mm});
            skLineSegment(sketch, "E294", {"start": v(91.33, -37.85) * mm, "end": v(91.72, -38.58) * mm});
            skLineSegment(sketch, "E295", {"start": v(91.72, -38.58) * mm, "end": v(91.02, -39) * mm});
            skLineSegment(sketch, "E296", {"start": v(91.02, -39) * mm, "end": v(90.72, -39.28) * mm});
            skLineSegment(sketch, "E297", {"start": v(90.72, -39.28) * mm, "end": v(90.46, -39.62) * mm});
            skLineSegment(sketch, "E298", {"start": v(90.46, -39.62) * mm, "end": v(90.23, -40) * mm});
            skLineSegment(sketch, "E299", {"start": v(90.23, -40) * mm, "end": v(90.02, -40.42) * mm});
            skLineSegment(sketch, "E300", {"start": v(90.02, -40.42) * mm, "end": v(89.85, -40.86) * mm});
            skLineSegment(sketch, "E301", {"start": v(89.85, -40.86) * mm, "end": v(90.42, -41.58) * mm});
            skLineSegment(sketch, "E302", {"start": v(90.42, -41.58) * mm, "end": v(90.9, -41.5) * mm});
            skLineSegment(sketch, "E303", {"start": v(90.9, -41.5) * mm, "end": v(91.34, -41.4) * mm});
            skLineSegment(sketch, "E304", {"start": v(91.34, -41.4) * mm, "end": v(91.77, -41.26) * mm});
            skLineSegment(sketch, "E305", {"start": v(91.77, -41.26) * mm, "end": v(92.15, -41.08) * mm});
            skLineSegment(sketch, "E306", {"start": v(92.15, -41.08) * mm, "end": v(92.5, -40.85) * mm});
            skLineSegment(sketch, "E307", {"start": v(92.5, -40.85) * mm, "end": v(93.06, -40.26) * mm});
            skLineSegment(sketch, "E308", {"start": v(93.06, -40.26) * mm, "end": v(93.68, -40.8) * mm});
            skLineSegment(sketch, "E309", {"start": v(93.68, -40.8) * mm, "end": v(93.68, -40.8) * mm});
            skLineSegment(sketch, "E310", {"start": v(93.68, -40.8) * mm, "end": v(94.35, -41.29) * mm});
            skLineSegment(sketch, "E311", {"start": v(94.35, -41.29) * mm, "end": v(93.9, -41.97) * mm});
            skLineSegment(sketch, "E312", {"start": v(93.9, -41.97) * mm, "end": v(93.75, -42.36) * mm});
            skLineSegment(sketch, "E313", {"start": v(93.75, -42.36) * mm, "end": v(93.66, -42.77) * mm});
            skLineSegment(sketch, "E314", {"start": v(93.66, -42.77) * mm, "end": v(93.62, -43.22) * mm});
            skLineSegment(sketch, "E315", {"start": v(93.62, -43.22) * mm, "end": v(93.62, -43.68) * mm});
            skLineSegment(sketch, "E316", {"start": v(93.62, -43.68) * mm, "end": v(93.65, -44.16) * mm});
            skLineSegment(sketch, "E317", {"start": v(93.65, -44.16) * mm, "end": v(94.48, -44.56) * mm});
            skLineSegment(sketch, "E318", {"start": v(94.48, -44.56) * mm, "end": v(94.87, -44.29) * mm});
            skLineSegment(sketch, "E319", {"start": v(94.87, -44.29) * mm, "end": v(95.24, -44) * mm});
            skLineSegment(sketch, "E320", {"start": v(95.24, -44) * mm, "end": v(95.55, -43.68) * mm});
            skLineSegment(sketch, "E321", {"start": v(95.55, -43.68) * mm, "end": v(95.83, -43.35) * mm});
            skLineSegment(sketch, "E322", {"start": v(95.83, -43.35) * mm, "end": v(96.03, -43) * mm});
            skLineSegment(sketch, "E323", {"start": v(96.03, -43) * mm, "end": v(96.29, -42.22) * mm});
            skLineSegment(sketch, "E324", {"start": v(96.29, -42.22) * mm, "end": v(97.08, -42.45) * mm});
            skLineSegment(sketch, "E325", {"start": v(97.08, -42.45) * mm, "end": v(97.08, -42.45) * mm});
            skLineSegment(sketch, "E326", {"start": v(98.97, -2.1) * mm, "end": v(98.97, 13.76) * mm});
            skArc(sketch, "E327", {"start": v(98.97, -2.1) * mm, "mid": v(99.35, -4.02) * mm, "end": v(100.44, -5.64) * mm});
            skLineSegment(sketch, "E328", {"start": v(106.97, -31.24) * mm, "end": v(106.97, -14.24) * mm});
            skArc(sketch, "E329", {"start": v(106.97, -14.24) * mm, "mid": v(106.6, -12.33) * mm, "end": v(105.5, -10.7) * mm});
            skLineSegment(sketch, "E330", {"start": v(108.97, 25.83) * mm, "end": v(108.97, 40.83) * mm});
            skLineSegment(sketch, "E331", {"start": v(108.97, 40.83) * mm, "end": v(106.04, 40.83) * mm});
            skArc(sketch, "E332", {"start": v(106.04, 40.83) * mm, "mid": v(104.13, 40.45) * mm, "end": v(102.5, 39.36) * mm});
            skLineSegment(sketch, "E333", {"start": v(88.96, -37.38) * mm, "end": v(88.97, 23.76) * mm});
            skLineSegment(sketch, "E334", {"start": v(102.5, 39.36) * mm, "end": v(90.43, 27.3) * mm});
            skArc(sketch, "E335", {"start": v(90.43, 27.3) * mm, "mid": v(89.35, 25.67) * mm, "end": v(88.97, 23.76) * mm});
            skLineSegment(sketch, "E336", {"start": v(108.97, 25.83) * mm, "end": v(100.44, 17.3) * mm});
            skArc(sketch, "E337", {"start": v(100.44, 17.3) * mm, "mid": v(99.35, 15.67) * mm, "end": v(98.97, 13.76) * mm});
            skLineSegment(sketch, "E338", {"start": v(100.44, -5.64) * mm, "end": v(105.5, -10.7) * mm});
            skLineSegment(sketch, "E339", {"start": v(104.32, -43.22) * mm, "end": v(104.28, -42.77) * mm});
            skLineSegment(sketch, "E340", {"start": v(103.6, -41.29) * mm, "end": v(104.26, -40.8) * mm});
            skLineSegment(sketch, "E341", {"start": v(104.26, -40.8) * mm, "end": v(104.26, -40.8) * mm});
            skLineSegment(sketch, "E342", {"start": v(104.26, -40.8) * mm, "end": v(104.88, -40.26) * mm});
            skLineSegment(sketch, "E343", {"start": v(105.45, -40.85) * mm, "end": v(105.79, -41.08) * mm});
            skLineSegment(sketch, "E344", {"start": v(106.18, -41.26) * mm, "end": v(106.6, -41.4) * mm});
            skLineSegment(sketch, "E345", {"start": v(107.05, -41.5) * mm, "end": v(107.52, -41.58) * mm});
            skLineSegment(sketch, "E346", {"start": v(107.52, -41.58) * mm, "end": v(108.1, -40.86) * mm});
            skLineSegment(sketch, "E347", {"start": v(108.1, -40.86) * mm, "end": v(107.92, -40.42) * mm});
            skLineSegment(sketch, "E348", {"start": v(107.48, -39.62) * mm, "end": v(107.22, -39.28) * mm});
            skLineSegment(sketch, "E349", {"start": v(107.22, -39.28) * mm, "end": v(106.92, -39) * mm});
            skLineSegment(sketch, "E350", {"start": v(106.22, -38.58) * mm, "end": v(106.62, -37.85) * mm});
            skLineSegment(sketch, "E351", {"start": v(106.62, -37.85) * mm, "end": v(106.62, -37.85) * mm});
            skLineSegment(sketch, "E352", {"start": v(106.62, -37.85) * mm, "end": v(106.94, -37.1) * mm});
            skLineSegment(sketch, "E353", {"start": v(107.7, -37.38) * mm, "end": v(108.1, -37.44) * mm});
            skLineSegment(sketch, "E354", {"start": v(108.1, -37.44) * mm, "end": v(108.54, -37.43) * mm});
            skLineSegment(sketch, "E355", {"start": v(108.54, -37.43) * mm, "end": v(108.98, -37.38) * mm});
            skLineSegment(sketch, "E356", {"start": v(108.98, -37.38) * mm, "end": v(109.43, -37.28) * mm});
            skLineSegment(sketch, "E357", {"start": v(109.43, -37.28) * mm, "end": v(109.9, -37.13) * mm});
            skLineSegment(sketch, "E358", {"start": v(109.9, -37.13) * mm, "end": v(110.1, -36.24) * mm});
            skLineSegment(sketch, "E359", {"start": v(110.1, -36.24) * mm, "end": v(109.74, -35.92) * mm});
            skLineSegment(sketch, "E360", {"start": v(109.74, -35.92) * mm, "end": v(109.38, -35.63) * mm});
            skLineSegment(sketch, "E361", {"start": v(109.38, -35.63) * mm, "end": v(109, -35.39) * mm});
            skLineSegment(sketch, "E362", {"start": v(109, -35.39) * mm, "end": v(108.62, -35.2) * mm});
            skLineSegment(sketch, "E363", {"start": v(108.62, -35.2) * mm, "end": v(108.23, -35.08) * mm});
            skLineSegment(sketch, "E364", {"start": v(108.23, -35.08) * mm, "end": v(107.42, -35) * mm});
            skLineSegment(sketch, "E365", {"start": v(107.42, -35) * mm, "end": v(107.46, -34.17) * mm});
            skLineSegment(sketch, "E366", {"start": v(107.46, -34.17) * mm, "end": v(107.46, -34.17) * mm});
            skLineSegment(sketch, "E367", {"start": v(107.46, -34.17) * mm, "end": v(107.42, -33.35) * mm});
            skLineSegment(sketch, "E368", {"start": v(107.42, -33.35) * mm, "end": v(108.23, -33.27) * mm});
            skLineSegment(sketch, "E369", {"start": v(108.23, -33.27) * mm, "end": v(108.62, -33.15) * mm});
            skLineSegment(sketch, "E370", {"start": v(108.62, -33.15) * mm, "end": v(109, -32.96) * mm});
            skLineSegment(sketch, "E371", {"start": v(109, -32.96) * mm, "end": v(109.38, -32.72) * mm});
            skLineSegment(sketch, "E372", {"start": v(109.38, -32.72) * mm, "end": v(109.74, -32.43) * mm});
            skLineSegment(sketch, "E373", {"start": v(109.74, -32.43) * mm, "end": v(110.1, -32.1) * mm});
            skLineSegment(sketch, "E374", {"start": v(110.1, -32.1) * mm, "end": v(109.9, -31.21) * mm});
            skLineSegment(sketch, "E375", {"start": v(109.9, -31.21) * mm, "end": v(109.43, -31.07) * mm});
            skLineSegment(sketch, "E376", {"start": v(109.43, -31.07) * mm, "end": v(108.98, -30.97) * mm});
            skLineSegment(sketch, "E377", {"start": v(108.98, -30.97) * mm, "end": v(108.54, -30.91) * mm});
            skLineSegment(sketch, "E378", {"start": v(108.54, -30.91) * mm, "end": v(108.1, -30.9) * mm});
            skLineSegment(sketch, "E379", {"start": v(108.1, -30.9) * mm, "end": v(107.7, -30.97) * mm});
            skLineSegment(sketch, "E380", {"start": v(107.7, -30.97) * mm, "end": v(106.97, -31.24) * mm});
            skLineSegment(sketch, "E381", {"start": v(150.9, -35.72) * mm, "end": v(151.04, -34.9) * mm});
            skLineSegment(sketch, "E382", {"start": v(151.04, -34.9) * mm, "end": v(151.85, -35) * mm});
            skLineSegment(sketch, "E383", {"start": v(151.85, -35) * mm, "end": v(152.25, -34.98) * mm});
            skLineSegment(sketch, "E384", {"start": v(152.25, -34.98) * mm, "end": v(152.62, -34.89) * mm});
            skLineSegment(sketch, "E385", {"start": v(132.98, -34.98) * mm, "end": v(133.4, -35) * mm});
            skLineSegment(sketch, "E386", {"start": v(134.2, -34.9) * mm, "end": v(134.35, -35.72) * mm});
            skLineSegment(sketch, "E387", {"start": v(133.8, -36.77) * mm, "end": v(133.44, -36.97) * mm});
            skLineSegment(sketch, "E388", {"start": v(132.8, -37.56) * mm, "end": v(132.5, -37.92) * mm});
            skLineSegment(sketch, "E389", {"start": v(133.57, -39.18) * mm, "end": v(134.02, -39.13) * mm});
            skLineSegment(sketch, "E390", {"start": v(134.02, -39.13) * mm, "end": v(134.44, -39.04) * mm});
            skLineSegment(sketch, "E391", {"start": v(134.44, -39.04) * mm, "end": v(134.82, -38.9) * mm});
            skLineSegment(sketch, "E392", {"start": v(134.82, -38.9) * mm, "end": v(135.5, -38.45) * mm});
            skLineSegment(sketch, "E393", {"start": v(135.5, -38.45) * mm, "end": v(135.98, -39.12) * mm});
            skLineSegment(sketch, "E394", {"start": v(135.98, -39.12) * mm, "end": v(135.98, -39.12) * mm});
            skLineSegment(sketch, "E395", {"start": v(136.53, -39.74) * mm, "end": v(135.94, -40.3) * mm});
            skLineSegment(sketch, "E396", {"start": v(135.28, -41.9) * mm, "end": v(135.21, -42.38) * mm});
            skLineSegment(sketch, "E397", {"start": v(135.21, -42.38) * mm, "end": v(135.93, -42.95) * mm});
            skLineSegment(sketch, "E398", {"start": v(135.93, -42.95) * mm, "end": v(136.37, -42.78) * mm});
            skLineSegment(sketch, "E399", {"start": v(136.8, -42.57) * mm, "end": v(137.17, -42.34) * mm});
            skLineSegment(sketch, "E400", {"start": v(137.17, -42.34) * mm, "end": v(137.5, -42.08) * mm});
            skLineSegment(sketch, "E401", {"start": v(137.79, -41.78) * mm, "end": v(138.21, -41.08) * mm});
            skLineSegment(sketch, "E402", {"start": v(138.21, -41.08) * mm, "end": v(138.94, -41.47) * mm});
            skLineSegment(sketch, "E403", {"start": v(138.94, -41.47) * mm, "end": v(138.94, -41.47) * mm});
            skLineSegment(sketch, "E404", {"start": v(139.7, -41.8) * mm, "end": v(139.42, -42.56) * mm});
            skLineSegment(sketch, "E405", {"start": v(139.51, -44.29) * mm, "end": v(139.66, -44.75) * mm});
            skLineSegment(sketch, "E406", {"start": v(140.55, -44.95) * mm, "end": v(140.88, -44.6) * mm});
            skLineSegment(sketch, "E407", {"start": v(141.16, -44.23) * mm, "end": v(141.4, -43.86) * mm});
            skLineSegment(sketch, "E408", {"start": v(141.8, -42.27) * mm, "end": v(142.62, -42.31) * mm});
            skLineSegment(sketch, "E409", {"start": v(142.62, -42.31) * mm, "end": v(142.62, -42.31) * mm});
            skLineSegment(sketch, "E410", {"start": v(142.62, -42.31) * mm, "end": v(143.44, -42.27) * mm});
            skLineSegment(sketch, "E411", {"start": v(143.44, -42.27) * mm, "end": v(143.52, -43.09) * mm});
            skLineSegment(sketch, "E412", {"start": v(143.52, -43.09) * mm, "end": v(143.64, -43.48) * mm});
            skLineSegment(sketch, "E413", {"start": v(143.64, -43.48) * mm, "end": v(143.83, -43.86) * mm});
            skLineSegment(sketch, "E414", {"start": v(143.83, -43.86) * mm, "end": v(144.07, -44.23) * mm});
            skLineSegment(sketch, "E415", {"start": v(144.07, -44.23) * mm, "end": v(144.36, -44.6) * mm});
            skLineSegment(sketch, "E416", {"start": v(144.36, -44.6) * mm, "end": v(144.69, -44.95) * mm});
            skLineSegment(sketch, "E417", {"start": v(144.69, -44.95) * mm, "end": v(145.58, -44.75) * mm});
            skLineSegment(sketch, "E418", {"start": v(145.58, -44.75) * mm, "end": v(145.72, -44.29) * mm});
            skLineSegment(sketch, "E419", {"start": v(145.72, -44.29) * mm, "end": v(145.82, -43.84) * mm});
            skLineSegment(sketch, "E420", {"start": v(145.82, -43.84) * mm, "end": v(145.88, -43.4) * mm});
            skLineSegment(sketch, "E421", {"start": v(145.88, -43.4) * mm, "end": v(145.88, -42.97) * mm});
            skLineSegment(sketch, "E422", {"start": v(145.88, -42.97) * mm, "end": v(145.82, -42.56) * mm});
            skLineSegment(sketch, "E423", {"start": v(145.82, -42.56) * mm, "end": v(145.54, -41.8) * mm});
            skLineSegment(sketch, "E424", {"start": v(145.54, -41.8) * mm, "end": v(146.3, -41.47) * mm});
            skLineSegment(sketch, "E425", {"start": v(146.3, -41.47) * mm, "end": v(146.3, -41.47) * mm});
            skLineSegment(sketch, "E426", {"start": v(146.3, -41.47) * mm, "end": v(147.03, -41.08) * mm});
            skLineSegment(sketch, "E427", {"start": v(147.03, -41.08) * mm, "end": v(147.45, -41.78) * mm});
            skLineSegment(sketch, "E428", {"start": v(147.45, -41.78) * mm, "end": v(147.73, -42.08) * mm});
            skLineSegment(sketch, "E429", {"start": v(147.73, -42.08) * mm, "end": v(148.07, -42.34) * mm});
            skLineSegment(sketch, "E430", {"start": v(148.07, -42.34) * mm, "end": v(148.45, -42.57) * mm});
            skLineSegment(sketch, "E431", {"start": v(148.45, -42.57) * mm, "end": v(148.86, -42.78) * mm});
            skLineSegment(sketch, "E432", {"start": v(148.86, -42.78) * mm, "end": v(149.3, -42.95) * mm});
            skLineSegment(sketch, "E433", {"start": v(149.3, -42.95) * mm, "end": v(150.02, -42.38) * mm});
            skLineSegment(sketch, "E434", {"start": v(150.02, -42.38) * mm, "end": v(149.95, -41.9) * mm});
            skLineSegment(sketch, "E435", {"start": v(149.95, -41.9) * mm, "end": v(149.85, -41.45) * mm});
            skLineSegment(sketch, "E436", {"start": v(149.85, -41.45) * mm, "end": v(149.7, -41.03) * mm});
            skLineSegment(sketch, "E437", {"start": v(149.7, -41.03) * mm, "end": v(149.53, -40.64) * mm});
            skLineSegment(sketch, "E438", {"start": v(149.53, -40.64) * mm, "end": v(149.3, -40.3) * mm});
            skLineSegment(sketch, "E439", {"start": v(149.3, -40.3) * mm, "end": v(148.7, -39.74) * mm});
            skLineSegment(sketch, "E440", {"start": v(148.7, -39.74) * mm, "end": v(149.25, -39.12) * mm});
            skLineSegment(sketch, "E441", {"start": v(149.25, -39.12) * mm, "end": v(149.25, -39.12) * mm});
            skLineSegment(sketch, "E442", {"start": v(149.25, -39.12) * mm, "end": v(149.73, -38.45) * mm});
            skLineSegment(sketch, "E443", {"start": v(149.73, -38.45) * mm, "end": v(150.42, -38.9) * mm});
            skLineSegment(sketch, "E444", {"start": v(150.42, -38.9) * mm, "end": v(150.8, -39.04) * mm});
            skLineSegment(sketch, "E445", {"start": v(150.8, -39.04) * mm, "end": v(151.22, -39.13) * mm});
            skLineSegment(sketch, "E446", {"start": v(151.22, -39.13) * mm, "end": v(151.66, -39.18) * mm});
            skLineSegment(sketch, "E447", {"start": v(151.66, -39.18) * mm, "end": v(152.13, -39.18) * mm});
            skLineSegment(sketch, "E448", {"start": v(152.13, -39.18) * mm, "end": v(152.6, -39.14) * mm});
            skLineSegment(sketch, "E449", {"start": v(152.6, -39.14) * mm, "end": v(153, -38.32) * mm});
            skLineSegment(sketch, "E450", {"start": v(153, -38.32) * mm, "end": v(152.73, -37.92) * mm});
            skLineSegment(sketch, "E451", {"start": v(152.73, -37.92) * mm, "end": v(152.44, -37.56) * mm});
            skLineSegment(sketch, "E452", {"start": v(152.44, -37.56) * mm, "end": v(152.13, -37.24) * mm});
            skLineSegment(sketch, "E453", {"start": v(152.13, -37.24) * mm, "end": v(151.8, -36.97) * mm});
            skLineSegment(sketch, "E454", {"start": v(151.8, -36.97) * mm, "end": v(151.44, -36.77) * mm});
            skLineSegment(sketch, "E455", {"start": v(151.44, -36.77) * mm, "end": v(150.67, -36.5) * mm});
            skLineSegment(sketch, "E456", {"start": v(150.67, -36.5) * mm, "end": v(150.9, -35.71) * mm});
            skLineSegment(sketch, "E457", {"start": v(150.9, -35.71) * mm, "end": v(150.9, -35.72) * mm});
            skLineSegment(sketch, "E458", {"start": v(134.62, -28.68) * mm, "end": v(134.62, -13.9) * mm});
            skLineSegment(sketch, "E459", {"start": v(132.62, 26.17) * mm, "end": v(132.62, 41.17) * mm});
            skLineSegment(sketch, "E460", {"start": v(132.62, 41.17) * mm, "end": v(135.55, 41.17) * mm});
            skLineSegment(sketch, "E461", {"start": v(152.62, -34.89) * mm, "end": v(152.62, 24.1) * mm});
            skArc(sketch, "E462", {"start": v(152.62, 24.1) * mm, "mid": v(152.24, 26.02) * mm, "end": v(151.15, 27.64) * mm});
            skLineSegment(sketch, "E463", {"start": v(139.08, 39.7) * mm, "end": v(151.15, 27.64) * mm});
            skArc(sketch, "E464", {"start": v(139.08, 39.7) * mm, "mid": v(137.46, 40.8) * mm, "end": v(135.55, 41.17) * mm});
            skLineSegment(sketch, "E465", {"start": v(132.62, 26.17) * mm, "end": v(141.15, 17.64) * mm});
            skArc(sketch, "E466", {"start": v(142.62, 14.1) * mm, "mid": v(142.24, 16.02) * mm, "end": v(141.15, 17.64) * mm});
            skLineSegment(sketch, "E467", {"start": v(142.62, 14.1) * mm, "end": v(142.62, -1.76) * mm});
            skArc(sketch, "E468", {"start": v(141.15, -5.3) * mm, "mid": v(142.24, -3.67) * mm, "end": v(142.62, -1.76) * mm});
            skLineSegment(sketch, "E469", {"start": v(141.15, -5.3) * mm, "end": v(136.08, -10.36) * mm});
            skArc(sketch, "E470", {"start": v(136.08, -10.36) * mm, "mid": v(135, -11.98) * mm, "end": v(134.62, -13.9) * mm});
            skLineSegment(sketch, "E471", {"start": v(134.62, -28.68) * mm, "end": v(134.44, -28.6) * mm});
            skLineSegment(sketch, "E472", {"start": v(134.44, -28.6) * mm, "end": v(134.02, -28.52) * mm});
            skLineSegment(sketch, "E473", {"start": v(134.02, -28.52) * mm, "end": v(133.57, -28.48) * mm});
            skLineSegment(sketch, "E474", {"start": v(133.57, -28.48) * mm, "end": v(133.11, -28.47) * mm});
            skLineSegment(sketch, "E475", {"start": v(133.11, -28.47) * mm, "end": v(132.63, -28.51) * mm});
            skLineSegment(sketch, "E476", {"start": v(132.63, -28.51) * mm, "end": v(132.24, -29.33) * mm});
            skLineSegment(sketch, "E477", {"start": v(132.24, -29.33) * mm, "end": v(132.5, -29.73) * mm});
            skLineSegment(sketch, "E478", {"start": v(132.5, -29.73) * mm, "end": v(132.8, -30.1) * mm});
            skLineSegment(sketch, "E479", {"start": v(132.8, -30.1) * mm, "end": v(133.1, -30.41) * mm});
            skLineSegment(sketch, "E480", {"start": v(133.1, -30.41) * mm, "end": v(133.44, -30.68) * mm});
            skLineSegment(sketch, "E481", {"start": v(133.44, -30.68) * mm, "end": v(133.8, -30.89) * mm});
            skLineSegment(sketch, "E482", {"start": v(133.8, -30.89) * mm, "end": v(134.57, -31.14) * mm});
            skLineSegment(sketch, "E483", {"start": v(134.57, -31.14) * mm, "end": v(134.35, -31.94) * mm});
            skLineSegment(sketch, "E484", {"start": v(134.35, -31.94) * mm, "end": v(134.35, -31.94) * mm});
            skLineSegment(sketch, "E485", {"start": v(134.35, -31.94) * mm, "end": v(134.2, -32.75) * mm});
            skLineSegment(sketch, "E486", {"start": v(134.2, -32.75) * mm, "end": v(133.4, -32.65) * mm});
            skLineSegment(sketch, "E487", {"start": v(133.4, -32.65) * mm, "end": v(132.98, -32.68) * mm});
            skLineSegment(sketch, "E488", {"start": v(132.98, -32.68) * mm, "end": v(132.57, -32.78) * mm});
            skLineSegment(sketch, "E489", {"start": v(132.57, -32.78) * mm, "end": v(132.15, -32.93) * mm});
            skLineSegment(sketch, "E490", {"start": v(132.15, -32.93) * mm, "end": v(131.73, -33.13) * mm});
            skLineSegment(sketch, "E491", {"start": v(131.73, -33.13) * mm, "end": v(131.31, -33.37) * mm});
            skLineSegment(sketch, "E492", {"start": v(131.31, -34.28) * mm, "end": v(131.73, -34.52) * mm});
            skLineSegment(sketch, "E493", {"start": v(131.73, -34.52) * mm, "end": v(132.15, -34.72) * mm});
            skLineSegment(sketch, "E494", {"start": v(132.15, -34.72) * mm, "end": v(132.57, -34.88) * mm});
            skLineSegment(sketch, "E495", {"start": v(132.57, -34.88) * mm, "end": v(132.98, -34.98) * mm});
            skLineSegment(sketch, "E496", {"start": v(133.4, -35) * mm, "end": v(134.2, -34.9) * mm});
            skLineSegment(sketch, "E497", {"start": v(134.35, -35.72) * mm, "end": v(134.35, -35.71) * mm});
            skLineSegment(sketch, "E498", {"start": v(134.35, -35.71) * mm, "end": v(134.57, -36.5) * mm});
            skLineSegment(sketch, "E499", {"start": v(134.57, -36.5) * mm, "end": v(133.8, -36.77) * mm});
            skLineSegment(sketch, "E500", {"start": v(133.44, -36.97) * mm, "end": v(133.1, -37.24) * mm});
            skLineSegment(sketch, "E501", {"start": v(133.1, -37.24) * mm, "end": v(132.8, -37.56) * mm});
            skLineSegment(sketch, "E502", {"start": v(132.5, -37.92) * mm, "end": v(132.24, -38.32) * mm});
            skLineSegment(sketch, "E503", {"start": v(132.24, -38.32) * mm, "end": v(132.63, -39.14) * mm});
            skLineSegment(sketch, "E504", {"start": v(132.63, -39.14) * mm, "end": v(133.11, -39.18) * mm});
            skLineSegment(sketch, "E505", {"start": v(133.11, -39.18) * mm, "end": v(133.57, -39.18) * mm});
            skLineSegment(sketch, "E506", {"start": v(135.98, -39.12) * mm, "end": v(136.53, -39.74) * mm});
            skLineSegment(sketch, "E507", {"start": v(135.94, -40.3) * mm, "end": v(135.71, -40.64) * mm});
            skLineSegment(sketch, "E508", {"start": v(135.71, -40.64) * mm, "end": v(135.53, -41.03) * mm});
            skLineSegment(sketch, "E509", {"start": v(135.53, -41.03) * mm, "end": v(135.39, -41.45) * mm});
            skLineSegment(sketch, "E510", {"start": v(135.39, -41.45) * mm, "end": v(135.28, -41.9) * mm});
            skLineSegment(sketch, "E511", {"start": v(136.37, -42.78) * mm, "end": v(136.8, -42.57) * mm});
            skLineSegment(sketch, "E512", {"start": v(137.5, -42.08) * mm, "end": v(137.79, -41.78) * mm});
            skLineSegment(sketch, "E513", {"start": v(138.94, -41.47) * mm, "end": v(139.7, -41.8) * mm});
            skLineSegment(sketch, "E514", {"start": v(139.42, -42.56) * mm, "end": v(139.35, -42.97) * mm});
            skLineSegment(sketch, "E515", {"start": v(139.35, -42.97) * mm, "end": v(139.36, -43.4) * mm});
            skLineSegment(sketch, "E516", {"start": v(139.36, -43.4) * mm, "end": v(139.41, -43.84) * mm});
            skLineSegment(sketch, "E517", {"start": v(139.41, -43.84) * mm, "end": v(139.51, -44.29) * mm});
            skLineSegment(sketch, "E518", {"start": v(139.66, -44.75) * mm, "end": v(140.55, -44.95) * mm});
            skLineSegment(sketch, "E519", {"start": v(140.88, -44.6) * mm, "end": v(141.16, -44.23) * mm});
            skLineSegment(sketch, "E520", {"start": v(141.4, -43.86) * mm, "end": v(141.6, -43.48) * mm});
            skLineSegment(sketch, "E521", {"start": v(141.6, -43.48) * mm, "end": v(141.71, -43.09) * mm});
            skLineSegment(sketch, "E522", {"start": v(141.71, -43.09) * mm, "end": v(141.8, -42.27) * mm});
            skLineSegment(sketch, "E523", {"start": v(131.31, -33.37) * mm, "end": v(131.31, -34.28) * mm});
            skCircle(sketch, "E524", {"center": v(142.62, -33.83) * mm, "radius": 0.75 * mm});
            skCircle(sketch, "E525", {"center": v(98.97, -34.17) * mm, "radius": 2.22 * mm});
            skCircle(sketch, "E526", {"center": v(98.97, -26.05) * mm, "radius": 0.55 * mm});
            skPoint(sketch, "E527.endSnap0", {"position": v(-2, -18.52) * mm});
            skLineSegment(sketch, "E528", {"start": v(-2, -15.8) * mm, "end": v(-0.05, -15.8) * mm});
            skLineSegment(sketch, "E529", {"start": v(27.56, -15.7) * mm, "end": v(27.56, -5.9) * mm});
            skLineSegment(sketch, "E530", {"start": v(-0.05, -15.8) * mm, "end": v(-0.05, -6) * mm});
            skLineSegment(sketch, "E531.trimOffspring", {"start": v(27.56, -15.7) * mm, "end": v(29.5, -15.7) * mm});
            skPoint(sketch, "E532.orphan", {"position": v(-2, -10.02) * mm});
            skLineSegment(sketch, "E533", {"start": v(-0.05, 23) * mm, "end": v(-0.05, 30) * mm});
            skLineSegment(sketch, "E534", {"start": v(27.56, 23.1) * mm, "end": v(27.56, 30.1) * mm});
            skArc(sketch, "E535", {"start": v(47.5, 10.1) * mm, "mid": v(41.67, 24.23) * mm, "end": v(27.56, 30.1) * mm});
            skPoint(sketch, "E536.endSnap0", {"position": v(-0.05, 10) * mm});
            skLineSegment(sketch, "E537", {"start": v(-20, 10) * mm, "end": v(-20, -33.15) * mm});
            skArc(sketch, "E538.trimOffspring", {"start": v(-0.05, 30) * mm, "mid": v(-14.16, 24.12) * mm, "end": v(-20, 10) * mm});
            skArc(sketch, "E539.trimOffspring", {"start": v(35.52, 2.57) * mm, "mid": v(38.42, 11.48) * mm, "end": v(33.4, 19.4) * mm});
            skLineSegment(sketch, "E540", {"start": v(27.56, -5.9) * mm, "end": v(35.52, 2.57) * mm});
            skLineSegment(sketch, "E541", {"start": v(27.56, 23.1) * mm, "end": v(33.4, 19.4) * mm});
            skArc(sketch, "E542", {"start": v(37.03, 0.54) * mm, "mid": v(40.93, 11.55) * mm, "end": v(34.79, 21.48) * mm});
            skLineSegment(sketch, "E543.MirrorCS", {"start": v(-0.05, -9) * mm, "end": v(-9.52, 0.43) * mm});
            skLineSegment(sketch, "E544", {"start": v(27.56, 26.1) * mm, "end": v(34.79, 21.48) * mm});
            skLineSegment(sketch, "E545", {"start": v(37.03, 0.54) * mm, "end": v(27.56, -9) * mm});
            skLineSegment(sketch, "E546", {"start": v(-0.05, -6) * mm, "end": v(-0.05, 23) * mm});
            skLineSegment(sketch, "E547", {"start": v(27.56, 23.1) * mm, "end": v(27.56, -9) * mm});
            skLineSegment(sketch, "E548", {"start": v(-129.43, -31.07) * mm, "end": v(-129.43, -28.07) * mm});
            skLineSegment(sketch, "E549", {"start": v(-129.43, 0.93) * mm, "end": v(-129.43, 3.93) * mm});
            skArc(sketch, "E550", {"start": v(-92.35, -21.53) * mm, "mid": v(-88.45, -10.52) * mm, "end": v(-94.6, -0.6) * mm});
            skLineSegment(sketch, "E551.MirrorCS", {"start": v(-129.43, -31.07) * mm, "end": v(-138.9, -21.63) * mm});
            skLineSegment(sketch, "E552", {"start": v(-101.82, 4.04) * mm, "end": v(-94.6, -0.6) * mm});
            skArc(sketch, "E553.trimOffspring", {"start": v(-136.66, -0.7) * mm, "mid": v(-142.8, -10.63) * mm, "end": v(-138.9, -21.63) * mm});
            skLineSegment(sketch, "E554.MirrorCS", {"start": v(-129.43, 3.93) * mm, "end": v(-136.66, -0.7) * mm});
            skLineSegment(sketch, "E555", {"start": v(-92.35, -21.53) * mm, "end": v(-101.82, -31.06) * mm});
            skLineSegment(sketch, "E556", {"start": v(-129.43, -28.07) * mm, "end": v(-129.43, 0.93) * mm});
            skLineSegment(sketch, "E557", {"start": v(-101.82, 1.04) * mm, "end": v(-101.82, -31.06) * mm});
            skLineSegment(sketch, "E558", {"start": v(-101.82, 4.04) * mm, "end": v(-101.82, 1.04) * mm});
            skLineSegment(sketch, "E559", {"start": v(-20, 0) * mm, "end": v(-12.1, 15.98) * mm});
            skLineSegment(sketch, "E560", {"start": v(47.5, 10.1) * mm, "end": v(39.85, 15.58) * mm});
            skLineSegment(sketch, "E561", {"start": v(-10, -19.95) * mm, "end": v(-10, -29.95) * mm});
            skLineSegment(sketch, "E562.0", {"start": v(0.68, -5.31) * mm, "end": v(-7.28, 3.15) * mm});
            skArc(sketch, "E562.1", {"start": v(-5.36, 18.44) * mm, "mid": v(-9.92, 11.25) * mm, "end": v(-7.28, 3.15) * mm});
            skLineSegment(sketch, "E562.2", {"start": v(0.49, 22.16) * mm, "end": v(-5.36, 18.44) * mm});
            skLineSegment(sketch, "E563.0", {"start": v(26.83, -5.2) * mm, "end": v(34.8, 3.26) * mm});
            skArc(sketch, "E563.1", {"start": v(34.8, 3.26) * mm, "mid": v(37.43, 11.35) * mm, "end": v(32.87, 18.55) * mm});
            skLineSegment(sketch, "E563.2", {"start": v(27.02, 22.26) * mm, "end": v(32.87, 18.55) * mm});
            skLineSegment(sketch, "E564.0", {"start": v(0.66, -8.3) * mm, "end": v(-8.82, 1.14) * mm});
            skArc(sketch, "E564.1", {"start": v(-6.74, 20.53) * mm, "mid": v(-12.43, 11.33) * mm, "end": v(-8.82, 1.14) * mm});
            skLineSegment(sketch, "E564.2", {"start": v(0.49, 25.16) * mm, "end": v(-6.74, 20.53) * mm});
            skLineSegment(sketch, "E565", {"start": v(-12.1, 15.98) * mm, "end": v(-10.12, 17.33) * mm});
            skLineSegment(sketch, "E566", {"start": v(-0.05, 21.82) * mm, "end": v(-6.74, 20.53) * mm});
            skLineSegment(sketch, "E567", {"start": v(-0.05, -4.54) * mm, "end": v(-7, -0.68) * mm});
            skLineSegment(sketch, "E568", {"start": v(-27.5, 20.53) * mm, "end": v(-6.74, 20.53) * mm});
            skLineSegment(sketch, "E569", {"start": v(-27.5, -0.68) * mm, "end": v(-7, -0.68) * mm});
            skLineSegment(sketch, "E570", {"start": v(-27.5, 21.13) * mm, "end": v(-5.8, 21.13) * mm});
            skLineSegment(sketch, "E571", {"start": v(-27.5, -1.28) * mm, "end": v(-6.4, -1.28) * mm});
            skLineSegment(sketch, "E572", {"start": v(27.56, 23.1) * mm, "end": v(32.24, 23.1) * mm});
            skLineSegment(sketch, "E573", {"start": v(37.03, 0.54) * mm, "end": v(33.6, 0.54) * mm});
            skLineSegment(sketch, "E574", {"start": v(33.6, 0.54) * mm, "end": v(32.24, 0.54) * mm});
            skLineSegment(sketch, "E575", {"start": v(-17, 20.53) * mm, "end": v(-17, -0.68) * mm});
            skLineSegment(sketch, "E576", {"start": v(-27.5, -1.28) * mm, "end": v(-32.08, -1.28) * mm});
            skLineSegment(sketch, "E577", {"start": v(-32.08, -1.28) * mm, "end": v(-32.08, -0.68) * mm});
            skLineSegment(sketch, "E578", {"start": v(-32.08, -0.68) * mm, "end": v(-32.08, 20.53) * mm});
            skLineSegment(sketch, "E579", {"start": v(-32.08, 20.53) * mm, "end": v(-32.08, 21.13) * mm});
            skLineSegment(sketch, "E580", {"start": v(-32.08, 21.13) * mm, "end": v(-27.5, 21.13) * mm});
            skLineSegment(sketch, "E581", {"start": v(-32.08, 20.53) * mm, "end": v(-27.5, 20.53) * mm});
            skLineSegment(sketch, "E582", {"start": v(-32.08, -0.68) * mm, "end": v(-27.5, -0.68) * mm});
            skSolve(sketch);
        }
        {
            var Q0;
            Q0=makeQuery(id+"F0.imprint","IMPRINT",FACE,{"disambiguationData":[TD([[makeQuery(id+"F0.imprint","IMPRINT",EDGE,{"derivedFrom":sQuery(id+"F0.wireOp",EDGE,"E0")}),1.0]])]});
            var Q1;
            Q1=makeQuery(id+"F0.imprint","IMPRINT",FACE,{"disambiguationData":[TD([[makeQuery(id+"F0.imprint","IMPRINT",EDGE,{"derivedFrom":sQuery(id+"F0.wireOp",EDGE,"E117")}),1.0]])]});
            var Q2;
            {var subQ5=sQuery(id+"F0.wireOp",EDGE,"E543.MirrorCS");Q2=makeQuery(id+"F0.imprint","IMPRINT",FACE,{"disambiguationData":[TD([[makeQuery(id+"F0.imprint","IMPRINT",EDGE,{"derivedFrom":subQ5}),-1.0]])]});}
            var Q3;
            {var subQ7=sQuery(id+"F0.wireOp",EDGE,"E559");var subQ8=sQuery(id+"F0.wireOp",EDGE,"E537");var subQ9=makeQuery(id+"F0.imprint","INTERSECT",VERTEX,{"derivedFrom":[subQ8,subQ7]});Q3=makeQuery(id+"F0.imprint","IMPRINT",FACE,{"disambiguationData":[TD([[makeQuery(id+"F0.imprint","IMPRINT",EDGE,{"disambiguationData":[TD([[subQ9,-1.0]])],"derivedFrom":subQ8}),1.0]])]});}
            var Q4;
            {var subQ0=sQuery(id+"F0.wireOp",EDGE,"E565");Q4=makeQuery(id+"F0.imprint","IMPRINT",FACE,{"disambiguationData":[TD([[makeQuery(id+"F0.imprint","IMPRINT",EDGE,{"derivedFrom":subQ0}),-1.0]])]});}
            var Q5;
            {var subQ0=sQuery(id+"F0.wireOp",EDGE,"E571");var subQ1=sQuery(id+"F0.wireOp",EDGE,"E537");var subQ2=makeQuery(id+"F0.imprint","INTERSECT",VERTEX,{"derivedFrom":[subQ1,subQ0]});Q5=makeQuery(id+"F0.imprint","IMPRINT",FACE,{"disambiguationData":[TD([[makeQuery(id+"F0.imprint","IMPRINT",EDGE,{"disambiguationData":[TD([[subQ2,1.0]])],"derivedFrom":subQ1}),1.0]])]});}
            extrude(context, id + "F1", {"entities" : qUnion([Q0, Q1, Q2, Q3, Q4, Q5]), "endBound" : BoundingType.SYMMETRIC, "depth" : 3 * mm, "offsetDistance" : 25 * mm});
        }
        {
            var Q0;
            {var subQ12=sQuery(id+"F0.wireOp",EDGE,"E562.1");Q0=makeQuery(id+"F0.imprint","IMPRINT",FACE,{"disambiguationData":[TD([[makeQuery(id+"F0.imprint","IMPRINT",EDGE,{"derivedFrom":subQ12}),-1.0]])]});}
            var Q1;
            Q1=makeQuery(id+"F0.imprint","IMPRINT",FACE,{"disambiguationData":[TD([[makeQuery(id+"F0.imprint","IMPRINT",EDGE,{"derivedFrom":sQuery(id+"F0.wireOp",EDGE,"E539.trimOffspring")}),1.0]])]});
            var Q2;
            Q2=makeQuery(id+"F0.imprint","IMPRINT",FACE,{"disambiguationData":[TD([[makeQuery(id+"F0.imprint","IMPRINT",EDGE,{"derivedFrom":sQuery(id+"F0.wireOp",EDGE,"E539.trimOffspring")}),-1.0]])]});
            var Q3;
            {var subQ5=sQuery(id+"F0.wireOp",EDGE,"E566");Q3=makeQuery(id+"F0.imprint","IMPRINT",FACE,{"disambiguationData":[TD([[makeQuery(id+"F0.imprint","IMPRINT",EDGE,{"derivedFrom":subQ5}),-1.0]])]});}
            var Q4;
            {var subQ5=sQuery(id+"F0.wireOp",EDGE,"E567");Q4=makeQuery(id+"F0.imprint","IMPRINT",FACE,{"disambiguationData":[TD([[makeQuery(id+"F0.imprint","IMPRINT",EDGE,{"derivedFrom":subQ5}),1.0]])]});}
            var Q5;
            {var subQ5=sQuery(id+"F0.wireOp",EDGE,"E562.1");Q5=makeQuery(id+"F0.imprint","IMPRINT",FACE,{"disambiguationData":[TD([[makeQuery(id+"F0.imprint","IMPRINT",EDGE,{"derivedFrom":subQ5}),1.0]])]});}
            var Q6;
            {var subQ5=sQuery(id+"F0.wireOp",EDGE,"E563.1");Q6=makeQuery(id+"F0.imprint","IMPRINT",FACE,{"disambiguationData":[TD([[makeQuery(id+"F0.imprint","IMPRINT",EDGE,{"derivedFrom":subQ5}),1.0]])]});}
            var Q7;
            {var subQ0=sQuery(id+"F0.wireOp",EDGE,"E565");Q7=makeQuery(id+"F0.imprint","IMPRINT",FACE,{"disambiguationData":[TD([[makeQuery(id+"F0.imprint","IMPRINT",EDGE,{"derivedFrom":subQ0}),1.0]])]});}
            var Q8;
            {var subQ5=sQuery(id+"F0.wireOp",EDGE,"DwxZqrDO-eQCU-IZmu-xYgW-qZ3TK6eNHvBr");Q8=makeQuery(id+"F0.imprint","IMPRINT",FACE,{"disambiguationData":[TD([[makeQuery(id+"F0.imprint","IMPRINT",EDGE,{"derivedFrom":subQ5}),-1.0]])]});}
            var Q9;
            {var subQ3=sQuery(id+"F0.wireOp",EDGE,"H77j5t0A-jiD4-WhC6-6j2W-TLOw7jgFkh7N");Q9=makeQuery(id+"F0.imprint","IMPRINT",FACE,{"disambiguationData":[TD([[makeQuery(id+"F0.imprint","IMPRINT",EDGE,{"derivedFrom":subQ3}),1.0]])]});}
            var Q10;
            {var subQ1=sQuery(id+"F0.wireOp",EDGE,"E537");var subQ3=sQuery(id+"F0.wireOp",EDGE,"E559");var subQ4=makeQuery(id+"F0.imprint","INTERSECT",VERTEX,{"derivedFrom":[subQ1,subQ3]});Q10=makeQuery(id+"F0.imprint","IMPRINT",FACE,{"disambiguationData":[TD([[makeQuery(id+"F0.imprint","IMPRINT",EDGE,{"disambiguationData":[TD([[subQ4,-1.0]])],"derivedFrom":subQ3}),1.0]])]});}
            var Q11;
            {var subQ7=sQuery(id+"F0.wireOp",EDGE,"E559");var subQ8=sQuery(id+"F0.wireOp",EDGE,"E537");var subQ9=makeQuery(id+"F0.imprint","INTERSECT",VERTEX,{"derivedFrom":[subQ8,subQ7]});Q11=makeQuery(id+"F0.imprint","IMPRINT",FACE,{"disambiguationData":[TD([[makeQuery(id+"F0.imprint","IMPRINT",EDGE,{"disambiguationData":[TD([[subQ9,-1.0]])],"derivedFrom":subQ8}),1.0]])]});}
            var Q12;
            {var subQ0=sQuery(id+"F0.wireOp",EDGE,"E565");Q12=makeQuery(id+"F0.imprint","IMPRINT",FACE,{"disambiguationData":[TD([[makeQuery(id+"F0.imprint","IMPRINT",EDGE,{"derivedFrom":subQ0}),-1.0]])]});}
            var Q13;
            {var subQ0=sQuery(id+"F0.wireOp",EDGE,"E570");var subQ1=sQuery(id+"F0.wireOp",EDGE,"E538.trimOffspring");var subQ2=makeQuery(id+"F0.imprint","INTERSECT",VERTEX,{"derivedFrom":[subQ1,subQ0]});Q13=makeQuery(id+"F0.imprint","IMPRINT",FACE,{"disambiguationData":[TD([[makeQuery(id+"F0.imprint","IMPRINT",EDGE,{"disambiguationData":[TD([[subQ2,-1.0]])],"derivedFrom":subQ1}),1.0]])]});}
            var Q14;
            {var subQ5=sQuery(id+"F0.wireOp",EDGE,"Lxmv7VKo-ALjP-86DP-BX1n-6o0UTrbWyWfY");Q14=makeQuery(id+"F0.imprint","IMPRINT",FACE,{"disambiguationData":[TD([[makeQuery(id+"F0.imprint","IMPRINT",EDGE,{"derivedFrom":subQ5}),-1.0]])]});}
            var Q15;
            {var subQ0=sQuery(id+"F0.wireOp",EDGE,"E569");var subQ1=sQuery(id+"F0.wireOp",EDGE,"E543.MirrorCS");var subQ2=makeQuery(id+"F0.imprint","INTERSECT",VERTEX,{"derivedFrom":[subQ1,subQ0]});Q15=makeQuery(id+"F0.imprint","IMPRINT",FACE,{"disambiguationData":[TD([[makeQuery(id+"F0.imprint","IMPRINT",EDGE,{"disambiguationData":[TD([[subQ2,1.0]])],"derivedFrom":subQ1}),-1.0]])]});}
            var Q16;
            {var subQ0=sQuery(id+"F0.wireOp",EDGE,"E571");var subQ1=sQuery(id+"F0.wireOp",EDGE,"E537");var subQ2=makeQuery(id+"F0.imprint","INTERSECT",VERTEX,{"derivedFrom":[subQ1,subQ0]});Q16=makeQuery(id+"F0.imprint","IMPRINT",FACE,{"disambiguationData":[TD([[makeQuery(id+"F0.imprint","IMPRINT",EDGE,{"disambiguationData":[TD([[subQ2,1.0]])],"derivedFrom":subQ1}),1.0]])]});}
            var Q17;
            {var subQ5=sQuery(id+"F0.wireOp",EDGE,"XuaBXOm0-JIJL-y1wx-34kB-GxtaGWgrbOUX");Q17=makeQuery(id+"F0.imprint","IMPRINT",FACE,{"disambiguationData":[TD([[makeQuery(id+"F0.imprint","IMPRINT",EDGE,{"derivedFrom":subQ5}),1.0]])]});}
            var Q18;
            {var subQ4=sQuery(id+"F0.wireOp",EDGE,"E545");Q18=makeQuery(id+"F0.imprint","IMPRINT",FACE,{"disambiguationData":[TD([[makeQuery(id+"F0.imprint","IMPRINT",EDGE,{"derivedFrom":subQ4}),-1.0]])]});}
            var Q19;
            {var subQ3=sQuery(id+"F0.wireOp",EDGE,"E574");Q19=makeQuery(id+"F0.imprint","IMPRINT",FACE,{"disambiguationData":[TD([[makeQuery(id+"F0.imprint","IMPRINT",EDGE,{"derivedFrom":subQ3}),1.0]])]});}
            var Q20;
            {var subQ0=sQuery(id+"F0.wireOp",EDGE,"E572");Q20=makeQuery(id+"F0.imprint","IMPRINT",FACE,{"disambiguationData":[TD([[makeQuery(id+"F0.imprint","IMPRINT",EDGE,{"derivedFrom":subQ0}),1.0]])]});}
            var Q21;
            Q21=makeQuery(id+"F0.imprint","IMPRINT",FACE,{"disambiguationData":[TD([[makeQuery(id+"F0.imprint","IMPRINT",EDGE,{"derivedFrom":sQuery(id+"F0.wireOp",EDGE,"E579")}),-1.0]])]});
            var Q22;
            {var subQ0=sQuery(id+"F0.wireOp",EDGE,"E576");Q22=makeQuery(id+"F0.imprint","IMPRINT",FACE,{"disambiguationData":[TD([[makeQuery(id+"F0.imprint","IMPRINT",EDGE,{"derivedFrom":subQ0}),-1.0]])]});}
            extrude(context, id + "F2", {"entities" : qUnion([Q0, Q1, Q2, Q3, Q4, Q5, Q6, Q7, Q8, Q9, Q10, Q11, Q12, Q13, Q14, Q15, Q16, Q17, Q18, Q19, Q20, Q21, Q22]), "depth" : 50 * mm, "offsetDistance" : 25 * mm});
        }
        {
            var Q0;
            {var subQ12=sQuery(id+"F0.wireOp",EDGE,"E562.1");Q0=makeQuery(id+"F0.imprint","IMPRINT",FACE,{"disambiguationData":[TD([[makeQuery(id+"F0.imprint","IMPRINT",EDGE,{"derivedFrom":subQ12}),-1.0]])]});}
            var Q1;
            Q1=makeQuery(id+"F0.imprint","IMPRINT",FACE,{"disambiguationData":[TD([[makeQuery(id+"F0.imprint","IMPRINT",EDGE,{"derivedFrom":sQuery(id+"F0.wireOp",EDGE,"E539.trimOffspring")}),1.0]])]});
            var Q2;
            Q2=makeQuery(id+"F0.imprint","IMPRINT",FACE,{"disambiguationData":[TD([[makeQuery(id+"F0.imprint","IMPRINT",EDGE,{"derivedFrom":sQuery(id+"F0.wireOp",EDGE,"E539.trimOffspring")}),-1.0]])]});
            var Q3;
            {var subQ5=sQuery(id+"F0.wireOp",EDGE,"E567");Q3=makeQuery(id+"F0.imprint","IMPRINT",FACE,{"disambiguationData":[TD([[makeQuery(id+"F0.imprint","IMPRINT",EDGE,{"derivedFrom":subQ5}),1.0]])]});}
            var Q4;
            {var subQ5=sQuery(id+"F0.wireOp",EDGE,"E566");Q4=makeQuery(id+"F0.imprint","IMPRINT",FACE,{"disambiguationData":[TD([[makeQuery(id+"F0.imprint","IMPRINT",EDGE,{"derivedFrom":subQ5}),-1.0]])]});}
            var Q5;
            {var subQ4=sQuery(id+"F0.wireOp",EDGE,"E545");Q5=makeQuery(id+"F0.imprint","IMPRINT",FACE,{"disambiguationData":[TD([[makeQuery(id+"F0.imprint","IMPRINT",EDGE,{"derivedFrom":subQ4}),-1.0]])]});}
            var Q6;
            {var subQ3=sQuery(id+"F0.wireOp",EDGE,"E574");Q6=makeQuery(id+"F0.imprint","IMPRINT",FACE,{"disambiguationData":[TD([[makeQuery(id+"F0.imprint","IMPRINT",EDGE,{"derivedFrom":subQ3}),1.0]])]});}
            var Q7;
            {var subQ0=sQuery(id+"F0.wireOp",EDGE,"E572");Q7=makeQuery(id+"F0.imprint","IMPRINT",FACE,{"disambiguationData":[TD([[makeQuery(id+"F0.imprint","IMPRINT",EDGE,{"derivedFrom":subQ0}),1.0]])]});}
            extrude(context, id + "F3", {"entities" : qUnion([Q0, Q1, Q2, Q3, Q4, Q5, Q6, Q7]), "operationType" : NewBodyOperationType.ADD, "oppositeDirection" : true, "depth" : 30 * mm, "offsetDistance" : 25 * mm});
        }
        {
            var Q0;
            {var subQ5=sQuery(id+"F0.wireOp",EDGE,"E562.1");Q0=makeQuery(id+"F0.imprint","IMPRINT",FACE,{"disambiguationData":[TD([[makeQuery(id+"F0.imprint","IMPRINT",EDGE,{"derivedFrom":subQ5}),-1.0]])]});}
            var Q1;
            {var subQ5=sQuery(id+"F0.wireOp",EDGE,"E562.1");Q1=makeQuery(id+"F0.imprint","IMPRINT",FACE,{"disambiguationData":[TD([[makeQuery(id+"F0.imprint","IMPRINT",EDGE,{"derivedFrom":subQ5}),1.0]])]});}
            var Q2;
            {var subQ5=sQuery(id+"F0.wireOp",EDGE,"E563.1");Q2=makeQuery(id+"F0.imprint","IMPRINT",FACE,{"disambiguationData":[TD([[makeQuery(id+"F0.imprint","IMPRINT",EDGE,{"derivedFrom":subQ5}),1.0]])]});}
            var Q3;
            {var subQ1=sQuery(id+"F0.wireOp",EDGE,"E537");var subQ3=sQuery(id+"F0.wireOp",EDGE,"E559");var subQ4=makeQuery(id+"F0.imprint","INTERSECT",VERTEX,{"derivedFrom":[subQ1,subQ3]});Q3=makeQuery(id+"F0.imprint","IMPRINT",FACE,{"disambiguationData":[TD([[makeQuery(id+"F0.imprint","IMPRINT",EDGE,{"disambiguationData":[TD([[subQ4,-1.0]])],"derivedFrom":subQ3}),1.0]])]});}
            var Q4;
            {var subQ7=sQuery(id+"F0.wireOp",EDGE,"E559");var subQ8=sQuery(id+"F0.wireOp",EDGE,"E537");var subQ9=makeQuery(id+"F0.imprint","INTERSECT",VERTEX,{"derivedFrom":[subQ8,subQ7]});Q4=makeQuery(id+"F0.imprint","IMPRINT",FACE,{"disambiguationData":[TD([[makeQuery(id+"F0.imprint","IMPRINT",EDGE,{"disambiguationData":[TD([[subQ9,-1.0]])],"derivedFrom":subQ8}),1.0]])]});}
            var Q5;
            {var subQ0=sQuery(id+"F0.wireOp",EDGE,"E565");Q5=makeQuery(id+"F0.imprint","IMPRINT",FACE,{"disambiguationData":[TD([[makeQuery(id+"F0.imprint","IMPRINT",EDGE,{"derivedFrom":subQ0}),-1.0]])]});}
            var Q6;
            {var subQ0=sQuery(id+"F0.wireOp",EDGE,"E565");Q6=makeQuery(id+"F0.imprint","IMPRINT",FACE,{"disambiguationData":[TD([[makeQuery(id+"F0.imprint","IMPRINT",EDGE,{"derivedFrom":subQ0}),1.0]])]});}
            var Q7;
            {var subQ0=sQuery(id+"F0.wireOp",EDGE,"E571");var subQ1=sQuery(id+"F0.wireOp",EDGE,"E537");var subQ2=makeQuery(id+"F0.imprint","INTERSECT",VERTEX,{"derivedFrom":[subQ1,subQ0]});Q7=makeQuery(id+"F0.imprint","IMPRINT",FACE,{"disambiguationData":[TD([[makeQuery(id+"F0.imprint","IMPRINT",EDGE,{"disambiguationData":[TD([[subQ2,1.0]])],"derivedFrom":subQ1}),1.0]])]});}
            var Q8;
            {var subQ0=sQuery(id+"F0.wireOp",EDGE,"E569");var subQ1=sQuery(id+"F0.wireOp",EDGE,"E543.MirrorCS");var subQ2=makeQuery(id+"F0.imprint","INTERSECT",VERTEX,{"derivedFrom":[subQ1,subQ0]});Q8=makeQuery(id+"F0.imprint","IMPRINT",FACE,{"disambiguationData":[TD([[makeQuery(id+"F0.imprint","IMPRINT",EDGE,{"disambiguationData":[TD([[subQ2,1.0]])],"derivedFrom":subQ1}),-1.0]])]});}
            var Q9;
            {var subQ0=sQuery(id+"F0.wireOp",EDGE,"E570");var subQ1=sQuery(id+"F0.wireOp",EDGE,"E538.trimOffspring");var subQ2=makeQuery(id+"F0.imprint","INTERSECT",VERTEX,{"derivedFrom":[subQ1,subQ0]});Q9=makeQuery(id+"F0.imprint","IMPRINT",FACE,{"disambiguationData":[TD([[makeQuery(id+"F0.imprint","IMPRINT",EDGE,{"disambiguationData":[TD([[subQ2,-1.0]])],"derivedFrom":subQ1}),1.0]])]});}
            var Q10;
            {var subQ5=sQuery(id+"F0.wireOp",EDGE,"XuaBXOm0-JIJL-y1wx-34kB-GxtaGWgrbOUX");Q10=makeQuery(id+"F0.imprint","IMPRINT",FACE,{"disambiguationData":[TD([[makeQuery(id+"F0.imprint","IMPRINT",EDGE,{"derivedFrom":subQ5}),1.0]])]});}
            var Q11;
            {var subQ5=sQuery(id+"F0.wireOp",EDGE,"Lxmv7VKo-ALjP-86DP-BX1n-6o0UTrbWyWfY");Q11=makeQuery(id+"F0.imprint","IMPRINT",FACE,{"disambiguationData":[TD([[makeQuery(id+"F0.imprint","IMPRINT",EDGE,{"derivedFrom":subQ5}),-1.0]])]});}
            var Q12;
            {var subQ4=sQuery(id+"F0.wireOp",EDGE,"E539.trimOffspring");Q12=makeQuery(id+"F0.imprint","IMPRINT",FACE,{"disambiguationData":[TD([[makeQuery(id+"F0.imprint","IMPRINT",EDGE,{"derivedFrom":subQ4}),-1.0]])]});}
            var Q13;
            {var subQ8=sQuery(id+"F0.wireOp",EDGE,"E539.trimOffspring");Q13=makeQuery(id+"F0.imprint","IMPRINT",FACE,{"disambiguationData":[TD([[makeQuery(id+"F0.imprint","IMPRINT",EDGE,{"derivedFrom":subQ8}),1.0]])]});}
            var Q14;
            Q14=makeQuery(id+"F0.imprint","IMPRINT",FACE,{"disambiguationData":[TD([[makeQuery(id+"F0.imprint","IMPRINT",EDGE,{"derivedFrom":sQuery(id+"F0.wireOp",EDGE,"E578")}),-1.0]])]});
            var Q15;
            {var subQ0=sQuery(id+"F0.wireOp",EDGE,"E576");Q15=makeQuery(id+"F0.imprint","IMPRINT",FACE,{"disambiguationData":[TD([[makeQuery(id+"F0.imprint","IMPRINT",EDGE,{"derivedFrom":subQ0}),-1.0]])]});}
            extrude(context, id + "F4", {"entities" : qUnion([Q0, Q1, Q2, Q3, Q4, Q5, Q6, Q7, Q8, Q9, Q10, Q11, Q12, Q13, Q14, Q15]), "operationType" : NewBodyOperationType.REMOVE, "depth" : 49 * mm, "offsetDistance" : 25 * mm});
        }
        {
            var Q0;
            {var subQ5=sQuery(id+"F0.wireOp",EDGE,"E562.1");Q0=makeQuery(id+"F0.imprint","IMPRINT",FACE,{"disambiguationData":[TD([[makeQuery(id+"F0.imprint","IMPRINT",EDGE,{"derivedFrom":subQ5}),-1.0]])]});}
            var Q1;
            {var subQ4=sQuery(id+"F0.wireOp",EDGE,"E539.trimOffspring");Q1=makeQuery(id+"F0.imprint","IMPRINT",FACE,{"disambiguationData":[TD([[makeQuery(id+"F0.imprint","IMPRINT",EDGE,{"derivedFrom":subQ4}),-1.0]])]});}
            var Q2;
            {var subQ8=sQuery(id+"F0.wireOp",EDGE,"E539.trimOffspring");Q2=makeQuery(id+"F0.imprint","IMPRINT",FACE,{"disambiguationData":[TD([[makeQuery(id+"F0.imprint","IMPRINT",EDGE,{"derivedFrom":subQ8}),1.0]])]});}
            var Q3;
            {var subQ0=sQuery(id+"F0.wireOp",EDGE,"E576");Q3=makeQuery(id+"F0.imprint","IMPRINT",FACE,{"disambiguationData":[TD([[makeQuery(id+"F0.imprint","IMPRINT",EDGE,{"derivedFrom":subQ0}),-1.0]])]});}
            extrude(context, id + "F5", {"entities" : qUnion([Q0, Q1, Q2, Q3]), "operationType" : NewBodyOperationType.ADD, "depth" : 46.8 * mm, "offsetDistance" : 25 * mm});
        }
        {
            var Q0;
            {var subQ7=sQuery(id+"F0.wireOp",EDGE,"E559");var subQ8=sQuery(id+"F0.wireOp",EDGE,"E537");var subQ9=makeQuery(id+"F0.imprint","INTERSECT",VERTEX,{"derivedFrom":[subQ8,subQ7]});Q0=makeQuery(id+"F0.imprint","IMPRINT",FACE,{"disambiguationData":[TD([[makeQuery(id+"F0.imprint","IMPRINT",EDGE,{"disambiguationData":[TD([[subQ9,-1.0]])],"derivedFrom":subQ8}),1.0]])]});}
            var Q1;
            {var subQ1=sQuery(id+"F0.wireOp",EDGE,"E537");var subQ3=sQuery(id+"F0.wireOp",EDGE,"E559");var subQ4=makeQuery(id+"F0.imprint","INTERSECT",VERTEX,{"derivedFrom":[subQ1,subQ3]});Q1=makeQuery(id+"F0.imprint","IMPRINT",FACE,{"disambiguationData":[TD([[makeQuery(id+"F0.imprint","IMPRINT",EDGE,{"disambiguationData":[TD([[subQ4,-1.0]])],"derivedFrom":subQ3}),1.0]])]});}
            var Q2;
            {var subQ0=sQuery(id+"F0.wireOp",EDGE,"E565");Q2=makeQuery(id+"F0.imprint","IMPRINT",FACE,{"disambiguationData":[TD([[makeQuery(id+"F0.imprint","IMPRINT",EDGE,{"derivedFrom":subQ0}),1.0]])]});}
            var Q3;
            {var subQ0=sQuery(id+"F0.wireOp",EDGE,"E565");Q3=makeQuery(id+"F0.imprint","IMPRINT",FACE,{"disambiguationData":[TD([[makeQuery(id+"F0.imprint","IMPRINT",EDGE,{"derivedFrom":subQ0}),-1.0]])]});}
            var Q4;
            Q4=makeQuery(id+"F0.imprint","IMPRINT",FACE,{"disambiguationData":[TD([[makeQuery(id+"F0.imprint","IMPRINT",EDGE,{"derivedFrom":sQuery(id+"F0.wireOp",EDGE,"E578")}),-1.0]])]});
            var Q5;
            {var subQ0=sQuery(id+"F0.wireOp",EDGE,"E576");Q5=makeQuery(id+"F0.imprint","IMPRINT",FACE,{"disambiguationData":[TD([[makeQuery(id+"F0.imprint","IMPRINT",EDGE,{"derivedFrom":subQ0}),-1.0]])]});}
            var Q6;
            {var subQ4=sQuery(id+"F0.wireOp",EDGE,"E537");var subQ6=sQuery(id+"F0.wireOp",EDGE,"E571");var subQ8=makeQuery(id+"F0.imprint","INTERSECT",VERTEX,{"derivedFrom":[subQ4,subQ6]});Q6=makeQuery(id+"F0.imprint","IMPRINT",FACE,{"disambiguationData":[TD([[makeQuery(id+"F0.imprint","IMPRINT",EDGE,{"disambiguationData":[TD([[subQ8,1.0]])],"derivedFrom":subQ4}),1.0]])]});}
            extrude(context, id + "F6", {"entities" : qUnion([Q0, Q1, Q2, Q3, Q4, Q5, Q6]), "operationType" : NewBodyOperationType.ADD, "depth" : 46.8 * mm, "offsetDistance" : 25 * mm});
        }
        {
            var Q0;
            {var subQ7=sQuery(id+"F0.wireOp",EDGE,"E559");var subQ8=sQuery(id+"F0.wireOp",EDGE,"E537");var subQ9=makeQuery(id+"F0.imprint","INTERSECT",VERTEX,{"derivedFrom":[subQ8,subQ7]});Q0=makeQuery(id+"F0.imprint","IMPRINT",FACE,{"disambiguationData":[TD([[makeQuery(id+"F0.imprint","IMPRINT",EDGE,{"disambiguationData":[TD([[subQ9,-1.0]])],"derivedFrom":subQ8}),1.0]])]});}
            var Q1;
            {var subQ0=sQuery(id+"F0.wireOp",EDGE,"E565");Q1=makeQuery(id+"F0.imprint","IMPRINT",FACE,{"disambiguationData":[TD([[makeQuery(id+"F0.imprint","IMPRINT",EDGE,{"derivedFrom":subQ0}),-1.0]])]});}
            var Q2;
            {var subQ1=sQuery(id+"F0.wireOp",EDGE,"E537");var subQ3=sQuery(id+"F0.wireOp",EDGE,"E559");var subQ4=makeQuery(id+"F0.imprint","INTERSECT",VERTEX,{"derivedFrom":[subQ1,subQ3]});Q2=makeQuery(id+"F0.imprint","IMPRINT",FACE,{"disambiguationData":[TD([[makeQuery(id+"F0.imprint","IMPRINT",EDGE,{"disambiguationData":[TD([[subQ4,-1.0]])],"derivedFrom":subQ3}),1.0]])]});}
            var Q3;
            {var subQ0=sQuery(id+"F0.wireOp",EDGE,"E565");Q3=makeQuery(id+"F0.imprint","IMPRINT",FACE,{"disambiguationData":[TD([[makeQuery(id+"F0.imprint","IMPRINT",EDGE,{"derivedFrom":subQ0}),1.0]])]});}
            var Q4;
            Q4=makeQuery(id+"F0.imprint","IMPRINT",FACE,{"disambiguationData":[TD([[makeQuery(id+"F0.imprint","IMPRINT",EDGE,{"derivedFrom":sQuery(id+"F0.wireOp",EDGE,"E578")}),-1.0]])]});
            var Q5;
            {var subQ0=sQuery(id+"F0.wireOp",EDGE,"E576");Q5=makeQuery(id+"F0.imprint","IMPRINT",FACE,{"disambiguationData":[TD([[makeQuery(id+"F0.imprint","IMPRINT",EDGE,{"derivedFrom":subQ0}),-1.0]])]});}
            var Q6;
            Q6=makeQuery(id+"F0.imprint","IMPRINT",FACE,{"disambiguationData":[TD([[makeQuery(id+"F0.imprint","IMPRINT",EDGE,{"derivedFrom":sQuery(id+"F0.wireOp",EDGE,"E579")}),-1.0]])]});
            extrude(context, id + "F7", {"entities" : qUnion([Q0, Q1, Q2, Q3, Q4, Q5, Q6]), "operationType" : NewBodyOperationType.REMOVE, "depth" : 45.8 * mm, "offsetDistance" : 25 * mm});
        }
        {
            var Q0;
            {var subQ0=sQuery(id+"F0.wireOp",EDGE,"E569");var subQ1=sQuery(id+"F0.wireOp",EDGE,"E543.MirrorCS");var subQ2=makeQuery(id+"F0.imprint","INTERSECT",VERTEX,{"derivedFrom":[subQ1,subQ0]});Q0=makeQuery(id+"F0.imprint","IMPRINT",FACE,{"disambiguationData":[TD([[makeQuery(id+"F0.imprint","IMPRINT",EDGE,{"disambiguationData":[TD([[subQ2,1.0]])],"derivedFrom":subQ1}),-1.0]])]});}
            var Q1;
            {var subQ0=sQuery(id+"F0.wireOp",EDGE,"E571");var subQ1=sQuery(id+"F0.wireOp",EDGE,"E537");var subQ2=makeQuery(id+"F0.imprint","INTERSECT",VERTEX,{"derivedFrom":[subQ1,subQ0]});Q1=makeQuery(id+"F0.imprint","IMPRINT",FACE,{"disambiguationData":[TD([[makeQuery(id+"F0.imprint","IMPRINT",EDGE,{"disambiguationData":[TD([[subQ2,1.0]])],"derivedFrom":subQ1}),1.0]])]});}
            var Q2;
            {var subQ5=sQuery(id+"F0.wireOp",EDGE,"XuaBXOm0-JIJL-y1wx-34kB-GxtaGWgrbOUX");Q2=makeQuery(id+"F0.imprint","IMPRINT",FACE,{"disambiguationData":[TD([[makeQuery(id+"F0.imprint","IMPRINT",EDGE,{"derivedFrom":subQ5}),1.0]])]});}
            var Q3;
            {var subQ0=sQuery(id+"F0.wireOp",EDGE,"E570");var subQ1=sQuery(id+"F0.wireOp",EDGE,"E538.trimOffspring");var subQ2=makeQuery(id+"F0.imprint","INTERSECT",VERTEX,{"derivedFrom":[subQ1,subQ0]});Q3=makeQuery(id+"F0.imprint","IMPRINT",FACE,{"disambiguationData":[TD([[makeQuery(id+"F0.imprint","IMPRINT",EDGE,{"disambiguationData":[TD([[subQ2,-1.0]])],"derivedFrom":subQ1}),1.0]])]});}
            var Q4;
            {var subQ5=sQuery(id+"F0.wireOp",EDGE,"Lxmv7VKo-ALjP-86DP-BX1n-6o0UTrbWyWfY");Q4=makeQuery(id+"F0.imprint","IMPRINT",FACE,{"disambiguationData":[TD([[makeQuery(id+"F0.imprint","IMPRINT",EDGE,{"derivedFrom":subQ5}),-1.0]])]});}
            extrude(context, id + "F8", {"entities" : qUnion([Q0, Q1, Q2, Q3, Q4]), "operationType" : NewBodyOperationType.ADD, "depth" : 49 * mm, "offsetDistance" : 25 * mm});
        }
        {
            var Q0;
            {var subQ0=sQuery(id+"F0.wireOp",EDGE,"E569");var subQ1=sQuery(id+"F0.wireOp",EDGE,"E543.MirrorCS");var subQ2=makeQuery(id+"F0.imprint","INTERSECT",VERTEX,{"derivedFrom":[subQ1,subQ0]});Q0=makeQuery(id+"F0.imprint","IMPRINT",FACE,{"disambiguationData":[TD([[makeQuery(id+"F0.imprint","IMPRINT",EDGE,{"disambiguationData":[TD([[subQ2,1.0]])],"derivedFrom":subQ1}),-1.0]])]});}
            var Q1;
            {var subQ0=sQuery(id+"F0.wireOp",EDGE,"E571");var subQ1=sQuery(id+"F0.wireOp",EDGE,"E537");var subQ2=makeQuery(id+"F0.imprint","INTERSECT",VERTEX,{"derivedFrom":[subQ1,subQ0]});Q1=makeQuery(id+"F0.imprint","IMPRINT",FACE,{"disambiguationData":[TD([[makeQuery(id+"F0.imprint","IMPRINT",EDGE,{"disambiguationData":[TD([[subQ2,1.0]])],"derivedFrom":subQ1}),1.0]])]});}
            var Q2;
            {var subQ5=sQuery(id+"F0.wireOp",EDGE,"XuaBXOm0-JIJL-y1wx-34kB-GxtaGWgrbOUX");Q2=makeQuery(id+"F0.imprint","IMPRINT",FACE,{"disambiguationData":[TD([[makeQuery(id+"F0.imprint","IMPRINT",EDGE,{"derivedFrom":subQ5}),1.0]])]});}
            var Q3;
            {var subQ0=sQuery(id+"F0.wireOp",EDGE,"E570");var subQ1=sQuery(id+"F0.wireOp",EDGE,"E538.trimOffspring");var subQ2=makeQuery(id+"F0.imprint","INTERSECT",VERTEX,{"derivedFrom":[subQ1,subQ0]});Q3=makeQuery(id+"F0.imprint","IMPRINT",FACE,{"disambiguationData":[TD([[makeQuery(id+"F0.imprint","IMPRINT",EDGE,{"disambiguationData":[TD([[subQ2,-1.0]])],"derivedFrom":subQ1}),1.0]])]});}
            var Q4;
            {var subQ5=sQuery(id+"F0.wireOp",EDGE,"Lxmv7VKo-ALjP-86DP-BX1n-6o0UTrbWyWfY");Q4=makeQuery(id+"F0.imprint","IMPRINT",FACE,{"disambiguationData":[TD([[makeQuery(id+"F0.imprint","IMPRINT",EDGE,{"derivedFrom":subQ5}),-1.0]])]});}
            extrude(context, id + "F9", {"entities" : qUnion([Q0, Q1, Q2, Q3, Q4]), "operationType" : NewBodyOperationType.REMOVE, "depth" : 45.8 * mm, "offsetDistance" : 25 * mm});
        }
        {
            var Q0;
            {var subQ7=sQuery(id+"F0.wireOp",EDGE,"E559");var subQ8=sQuery(id+"F0.wireOp",EDGE,"E537");var subQ9=makeQuery(id+"F0.imprint","INTERSECT",VERTEX,{"derivedFrom":[subQ8,subQ7]});Q0=makeQuery(id+"F0.imprint","IMPRINT",FACE,{"disambiguationData":[TD([[makeQuery(id+"F0.imprint","IMPRINT",EDGE,{"disambiguationData":[TD([[subQ9,-1.0]])],"derivedFrom":subQ8}),1.0]])]});}
            var Q1;
            {var subQ0=sQuery(id+"F0.wireOp",EDGE,"E565");Q1=makeQuery(id+"F0.imprint","IMPRINT",FACE,{"disambiguationData":[TD([[makeQuery(id+"F0.imprint","IMPRINT",EDGE,{"derivedFrom":subQ0}),-1.0]])]});}
            var Q2;
            {var subQ0=sQuery(id+"F0.wireOp",EDGE,"E571");var subQ1=sQuery(id+"F0.wireOp",EDGE,"E537");var subQ2=makeQuery(id+"F0.imprint","INTERSECT",VERTEX,{"derivedFrom":[subQ1,subQ0]});Q2=makeQuery(id+"F0.imprint","IMPRINT",FACE,{"disambiguationData":[TD([[makeQuery(id+"F0.imprint","IMPRINT",EDGE,{"disambiguationData":[TD([[subQ2,1.0]])],"derivedFrom":subQ1}),1.0]])]});}
            var Q3;
            {var subQ0=sQuery(id+"F0.wireOp",EDGE,"E569");var subQ1=sQuery(id+"F0.wireOp",EDGE,"E543.MirrorCS");var subQ2=makeQuery(id+"F0.imprint","INTERSECT",VERTEX,{"derivedFrom":[subQ1,subQ0]});Q3=makeQuery(id+"F0.imprint","IMPRINT",FACE,{"disambiguationData":[TD([[makeQuery(id+"F0.imprint","IMPRINT",EDGE,{"disambiguationData":[TD([[subQ2,1.0]])],"derivedFrom":subQ1}),-1.0]])]});}
            extrude(context, id + "F10", {"entities" : qUnion([Q0, Q1, Q2, Q3]), "operationType" : NewBodyOperationType.ADD, "depth" : 1.5 * mm, "offsetDistance" : 25 * mm});
        }
        {
            var Q0;
            Q0=makeQuery(id+"F2.opExtrude","CAP_FACE",FACE,{"disambiguationData":[OSD([sQuery(id+"F0.wireOp",EDGE,"E534"),sQuery(id+"F0.wireOp",EDGE,"E542"),sQuery(id+"F0.wireOp",EDGE,"E544"),sQuery(id+"F0.wireOp",EDGE,"E545"),sQuery(id+"F0.wireOp",EDGE,"E547")])],"isStart":false});
            var sketch = newSketch(context, id + "F11", { "sketchPlane" : qUnion([Q0])});
            skLineSegment(sketch, "E583", {"start": v(-83, 114.22) * mm, "end": v(-63.42, 114.22) * mm});
            skLineSegment(sketch, "E584", {"start": v(-83, 91.64) * mm, "end": v(-83, 92.28) * mm});
            skLineSegment(sketch, "E585", {"start": v(-83, 114.22) * mm, "end": v(-83, 113.46) * mm});
            skLineSegment(sketch, "E586", {"start": v(-63.42, 90.95) * mm, "end": v(-74.22, 90.95) * mm});
            skLineSegment(sketch, "E587", {"start": v(-63.42, 114.88) * mm, "end": v(-79.36, 114.88) * mm});
            skLineSegment(sketch, "E588", {"start": v(-63.42, 114.88) * mm, "end": v(-43.42, 114.88) * mm});
            skLineSegment(sketch, "E589", {"start": v(-43.42, 114.88) * mm, "end": v(-43.42, 114.22) * mm});
            skLineSegment(sketch, "E590", {"start": v(-43.42, 114.22) * mm, "end": v(-63.42, 114.22) * mm});
            skLineSegment(sketch, "E591", {"start": v(-43.42, 114.22) * mm, "end": v(-43.42, 91.64) * mm});
            skLineSegment(sketch, "E592", {"start": v(-63.42, 90.95) * mm, "end": v(-43.42, 90.95) * mm});
            skLineSegment(sketch, "E593", {"start": v(-43.42, 90.95) * mm, "end": v(-43.42, 91.64) * mm});
            skLineSegment(sketch, "E594", {"start": v(-63.42, 91.64) * mm, "end": v(-43.42, 91.64) * mm});
            skLineSegment(sketch, "E595", {"start": v(-63.42, 91.64) * mm, "end": v(-73.53, 91.64) * mm});
            skArc(sketch, "E596.0", {"start": v(-73.53, 91.64) * mm, "mid": v(-69.63, 102.65) * mm, "end": v(-75.77, 112.58) * mm});
            skLineSegment(sketch, "E597.0", {"start": v(-83, 117.21) * mm, "end": v(-75.77, 112.58) * mm});
            skLineSegment(sketch, "E598.0", {"start": v(-73.53, 91.64) * mm, "end": v(-83, 82.11) * mm});
            skSolve(sketch);
        }
        {
            var Q0;
            {var subQ3=sQuery(id+"F11.wireOp",EDGE,"E586");Q0=makeQuery(id+"F11.imprint","IMPRINT",FACE,{"disambiguationData":[TD([[makeQuery(id+"F11.imprint","IMPRINT",EDGE,{"derivedFrom":subQ3}),-1.0]])]});}
            var Q1;
            {var subQ0=sQuery(id+"F11.wireOp",EDGE,"E587");Q1=makeQuery(id+"F11.imprint","IMPRINT",FACE,{"disambiguationData":[TD([[makeQuery(id+"F11.imprint","IMPRINT",EDGE,{"derivedFrom":subQ0}),1.0]])]});}
            var Q2;
            Q2=makeQuery(id+"F11.imprint","IMPRINT",FACE,{"disambiguationData":[TD([[makeQuery(id+"F11.imprint","IMPRINT",EDGE,{"derivedFrom":sQuery(id+"F11.wireOp",EDGE,"E592")}),1.0]])]});
            var Q3;
            {var subQ0=sQuery(id+"F11.wireOp",EDGE,"E590");Q3=makeQuery(id+"F11.imprint","IMPRINT",FACE,{"disambiguationData":[TD([[makeQuery(id+"F11.imprint","IMPRINT",EDGE,{"derivedFrom":subQ0}),1.0]])]});}
            extrude(context, id + "F12", {"entities" : qUnion([Q0, Q1, Q2, Q3]), "operationType" : NewBodyOperationType.ADD, "oppositeDirection" : true, "depth" : 4 * mm, "offsetDistance" : 25 * mm});
        }
        {
            var Q0;
            {var subQ0=sQuery(id+"F11.wireOp",EDGE,"E590");Q0=makeQuery(id+"F11.imprint","IMPRINT",FACE,{"disambiguationData":[TD([[makeQuery(id+"F11.imprint","IMPRINT",EDGE,{"derivedFrom":subQ0}),1.0]])]});}
            extrude(context, id + "F13", {"entities" : qUnion([Q0]), "operationType" : NewBodyOperationType.REMOVE, "oppositeDirection" : true, "depth" : 3 * mm, "offsetDistance" : 25 * mm});
        }
        {
            var Q0;
            {var subQ0=sQuery(id+"F11.wireOp",EDGE,"E590");Q0=makeQuery(id+"F11.imprint","IMPRINT",FACE,{"disambiguationData":[TD([[makeQuery(id+"F11.imprint","IMPRINT",EDGE,{"derivedFrom":subQ0}),1.0]])]});}
            extrude(context, id + "F14", {"entities" : qUnion([Q0]), "operationType" : NewBodyOperationType.ADD, "oppositeDirection" : true, "depth" : 1 * mm, "offsetDistance" : 25 * mm});
        }
    });
